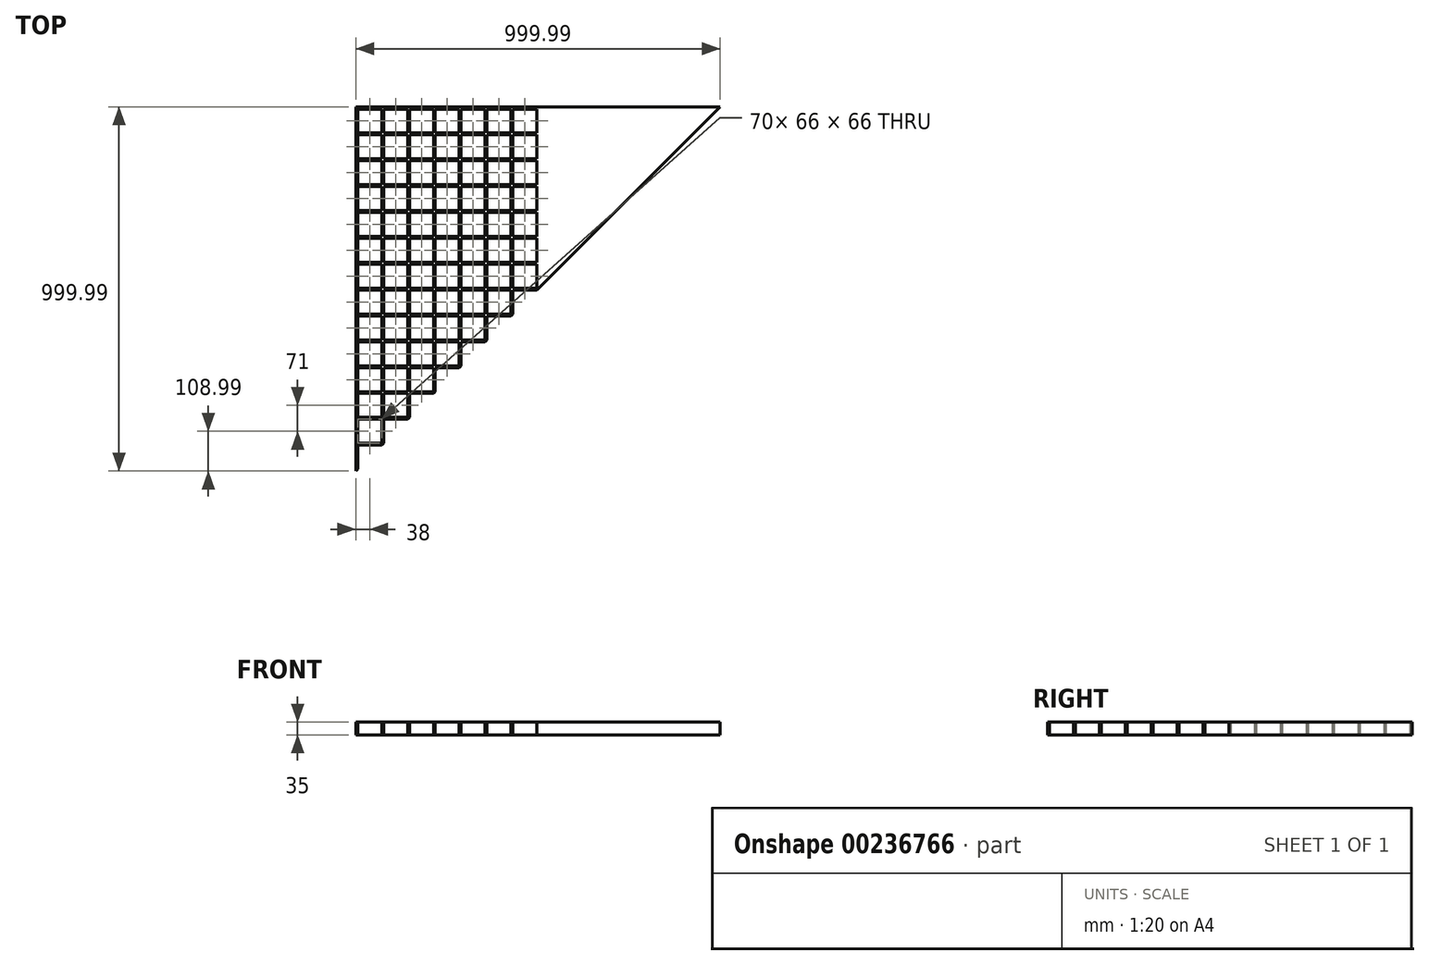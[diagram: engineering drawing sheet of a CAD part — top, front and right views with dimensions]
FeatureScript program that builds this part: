
annotation { "Feature Type Name" : "Feature", "Feature Type Description" : "" }
export const myFeature = defineFeature(function(context is Context, id is Id, definition is map)
    precondition{}
    {
        {
            var Q0;
            Q0=qCreatedBy(makeId("Top.planeOp"),FACE);
            var sketch = newSketch(context, id + "F0", { "sketchPlane" : qUnion([Q0])});
            skLineSegment(sketch, "E0.bottom", {"start": v(0, 0) * mm, "end": v(1000, 0) * mm});
            skLineSegment(sketch, "E0.top", {"start": v(0, 1000) * mm, "end": v(1000, 1000) * mm});
            skLineSegment(sketch, "E0.left", {"start": v(0, 0) * mm, "end": v(0, 1000) * mm});
            skLineSegment(sketch, "E0.right", {"start": v(1000, 0) * mm, "end": v(1000, 1000) * mm});
            skLineSegment(sketch, "E1.bottom", {"start": v(5, 5) * mm, "end": v(71, 5) * mm});
            skLineSegment(sketch, "E1.top", {"start": v(5, 71) * mm, "end": v(71, 71) * mm});
            skLineSegment(sketch, "E1.left", {"start": v(5, 5) * mm, "end": v(5, 71) * mm});
            skLineSegment(sketch, "E1.right", {"start": v(71, 5) * mm, "end": v(71, 71) * mm});
            skLineSegment(sketch, "E2.0.1.0", {"start": v(5, 142) * mm, "end": v(71, 142) * mm});
            skLineSegment(sketch, "E2.0.1.1", {"start": v(5, 76) * mm, "end": v(5, 142) * mm});
            skLineSegment(sketch, "E2.0.1.2", {"start": v(5, 76) * mm, "end": v(71, 76) * mm});
            skLineSegment(sketch, "E2.0.1.3", {"start": v(71, 76) * mm, "end": v(71, 142) * mm});
            skLineSegment(sketch, "E2.0.2.0", {"start": v(5, 213) * mm, "end": v(71, 213) * mm});
            skLineSegment(sketch, "E2.0.2.1", {"start": v(5, 147) * mm, "end": v(5, 213) * mm});
            skLineSegment(sketch, "E2.0.2.2", {"start": v(5, 147) * mm, "end": v(71, 147) * mm});
            skLineSegment(sketch, "E2.0.2.3", {"start": v(71, 147) * mm, "end": v(71, 213) * mm});
            skLineSegment(sketch, "E2.0.3.0", {"start": v(5, 284) * mm, "end": v(71, 284) * mm});
            skLineSegment(sketch, "E2.0.3.1", {"start": v(5, 218) * mm, "end": v(5, 284) * mm});
            skLineSegment(sketch, "E2.0.3.2", {"start": v(5, 218) * mm, "end": v(71, 218) * mm});
            skLineSegment(sketch, "E2.0.3.3", {"start": v(71, 218) * mm, "end": v(71, 284) * mm});
            skLineSegment(sketch, "E2.0.4.0", {"start": v(5, 355) * mm, "end": v(71, 355) * mm});
            skLineSegment(sketch, "E2.0.4.1", {"start": v(5, 289) * mm, "end": v(5, 355) * mm});
            skLineSegment(sketch, "E2.0.4.2", {"start": v(5, 289) * mm, "end": v(71, 289) * mm});
            skLineSegment(sketch, "E2.0.4.3", {"start": v(71, 289) * mm, "end": v(71, 355) * mm});
            skLineSegment(sketch, "E2.0.5.0", {"start": v(5, 426) * mm, "end": v(71, 426) * mm});
            skLineSegment(sketch, "E2.0.5.1", {"start": v(5, 360) * mm, "end": v(5, 426) * mm});
            skLineSegment(sketch, "E2.0.5.2", {"start": v(5, 360) * mm, "end": v(71, 360) * mm});
            skLineSegment(sketch, "E2.0.5.3", {"start": v(71, 360) * mm, "end": v(71, 426) * mm});
            skLineSegment(sketch, "E2.0.6.0", {"start": v(5, 497) * mm, "end": v(71, 497) * mm});
            skLineSegment(sketch, "E2.0.6.1", {"start": v(5, 431) * mm, "end": v(5, 497) * mm});
            skLineSegment(sketch, "E2.0.6.2", {"start": v(5, 431) * mm, "end": v(71, 431) * mm});
            skLineSegment(sketch, "E2.0.6.3", {"start": v(71, 431) * mm, "end": v(71, 497) * mm});
            skLineSegment(sketch, "E2.0.7.0", {"start": v(5, 568) * mm, "end": v(71, 568) * mm});
            skLineSegment(sketch, "E2.0.7.1", {"start": v(5, 502) * mm, "end": v(5, 568) * mm});
            skLineSegment(sketch, "E2.0.7.2", {"start": v(5, 502) * mm, "end": v(71, 502) * mm});
            skLineSegment(sketch, "E2.0.7.3", {"start": v(71, 502) * mm, "end": v(71, 568) * mm});
            skLineSegment(sketch, "E2.0.8.0", {"start": v(5, 639) * mm, "end": v(71, 639) * mm});
            skLineSegment(sketch, "E2.0.8.1", {"start": v(5, 573) * mm, "end": v(5, 639) * mm});
            skLineSegment(sketch, "E2.0.8.2", {"start": v(5, 573) * mm, "end": v(71, 573) * mm});
            skLineSegment(sketch, "E2.0.8.3", {"start": v(71, 573) * mm, "end": v(71, 639) * mm});
            skLineSegment(sketch, "E2.0.9.0", {"start": v(5, 710) * mm, "end": v(71, 710) * mm});
            skLineSegment(sketch, "E2.0.9.1", {"start": v(5, 644) * mm, "end": v(5, 710) * mm});
            skLineSegment(sketch, "E2.0.9.2", {"start": v(5, 644) * mm, "end": v(71, 644) * mm});
            skLineSegment(sketch, "E2.0.9.3", {"start": v(71, 644) * mm, "end": v(71, 710) * mm});
            skLineSegment(sketch, "E2.0.10.0", {"start": v(5, 781) * mm, "end": v(71, 781) * mm});
            skLineSegment(sketch, "E2.0.10.1", {"start": v(5, 715) * mm, "end": v(5, 781) * mm});
            skLineSegment(sketch, "E2.0.10.2", {"start": v(5, 715) * mm, "end": v(71, 715) * mm});
            skLineSegment(sketch, "E2.0.10.3", {"start": v(71, 715) * mm, "end": v(71, 781) * mm});
            skLineSegment(sketch, "E2.0.11.0", {"start": v(5, 852) * mm, "end": v(71, 852) * mm});
            skLineSegment(sketch, "E2.0.11.1", {"start": v(5, 786) * mm, "end": v(5, 852) * mm});
            skLineSegment(sketch, "E2.0.11.2", {"start": v(5, 786) * mm, "end": v(71, 786) * mm});
            skLineSegment(sketch, "E2.0.11.3", {"start": v(71, 786) * mm, "end": v(71, 852) * mm});
            skLineSegment(sketch, "E2.0.12.0", {"start": v(5, 923) * mm, "end": v(71, 923) * mm});
            skLineSegment(sketch, "E2.0.12.1", {"start": v(5, 857) * mm, "end": v(5, 923) * mm});
            skLineSegment(sketch, "E2.0.12.2", {"start": v(5, 857) * mm, "end": v(71, 857) * mm});
            skLineSegment(sketch, "E2.0.12.3", {"start": v(71, 857) * mm, "end": v(71, 923) * mm});
            skLineSegment(sketch, "E2.0.13.0", {"start": v(5, 994) * mm, "end": v(71, 994) * mm});
            skLineSegment(sketch, "E2.0.13.1", {"start": v(5, 928) * mm, "end": v(5, 994) * mm});
            skLineSegment(sketch, "E2.0.13.2", {"start": v(5, 928) * mm, "end": v(71, 928) * mm});
            skLineSegment(sketch, "E2.0.13.3", {"start": v(71, 928) * mm, "end": v(71, 994) * mm});
            skLineSegment(sketch, "E2.1.0.0", {"start": v(76, 71) * mm, "end": v(142, 71) * mm});
            skLineSegment(sketch, "E2.1.0.1", {"start": v(76, 5) * mm, "end": v(76, 71) * mm});
            skLineSegment(sketch, "E2.1.0.2", {"start": v(76, 5) * mm, "end": v(142, 5) * mm});
            skLineSegment(sketch, "E2.1.0.3", {"start": v(142, 5) * mm, "end": v(142, 71) * mm});
            skLineSegment(sketch, "E2.1.1.0", {"start": v(76, 142) * mm, "end": v(142, 142) * mm});
            skLineSegment(sketch, "E2.1.1.1", {"start": v(76, 76) * mm, "end": v(76, 142) * mm});
            skLineSegment(sketch, "E2.1.1.2", {"start": v(76, 76) * mm, "end": v(142, 76) * mm});
            skLineSegment(sketch, "E2.1.1.3", {"start": v(142, 76) * mm, "end": v(142, 142) * mm});
            skLineSegment(sketch, "E2.1.2.0", {"start": v(76, 213) * mm, "end": v(142, 213) * mm});
            skLineSegment(sketch, "E2.1.2.1", {"start": v(76, 147) * mm, "end": v(76, 213) * mm});
            skLineSegment(sketch, "E2.1.2.2", {"start": v(76, 147) * mm, "end": v(142, 147) * mm});
            skLineSegment(sketch, "E2.1.2.3", {"start": v(142, 147) * mm, "end": v(142, 213) * mm});
            skLineSegment(sketch, "E2.1.3.0", {"start": v(76, 284) * mm, "end": v(142, 284) * mm});
            skLineSegment(sketch, "E2.1.3.1", {"start": v(76, 218) * mm, "end": v(76, 284) * mm});
            skLineSegment(sketch, "E2.1.3.2", {"start": v(76, 218) * mm, "end": v(142, 218) * mm});
            skLineSegment(sketch, "E2.1.3.3", {"start": v(142, 218) * mm, "end": v(142, 284) * mm});
            skLineSegment(sketch, "E2.1.4.0", {"start": v(76, 355) * mm, "end": v(142, 355) * mm});
            skLineSegment(sketch, "E2.1.4.1", {"start": v(76, 289) * mm, "end": v(76, 355) * mm});
            skLineSegment(sketch, "E2.1.4.2", {"start": v(76, 289) * mm, "end": v(142, 289) * mm});
            skLineSegment(sketch, "E2.1.4.3", {"start": v(142, 289) * mm, "end": v(142, 355) * mm});
            skLineSegment(sketch, "E2.1.5.0", {"start": v(76, 426) * mm, "end": v(142, 426) * mm});
            skLineSegment(sketch, "E2.1.5.1", {"start": v(76, 360) * mm, "end": v(76, 426) * mm});
            skLineSegment(sketch, "E2.1.5.2", {"start": v(76, 360) * mm, "end": v(142, 360) * mm});
            skLineSegment(sketch, "E2.1.5.3", {"start": v(142, 360) * mm, "end": v(142, 426) * mm});
            skLineSegment(sketch, "E2.1.6.0", {"start": v(76, 497) * mm, "end": v(142, 497) * mm});
            skLineSegment(sketch, "E2.1.6.1", {"start": v(76, 431) * mm, "end": v(76, 497) * mm});
            skLineSegment(sketch, "E2.1.6.2", {"start": v(76, 431) * mm, "end": v(142, 431) * mm});
            skLineSegment(sketch, "E2.1.6.3", {"start": v(142, 431) * mm, "end": v(142, 497) * mm});
            skLineSegment(sketch, "E2.1.7.0", {"start": v(76, 568) * mm, "end": v(142, 568) * mm});
            skLineSegment(sketch, "E2.1.7.1", {"start": v(76, 502) * mm, "end": v(76, 568) * mm});
            skLineSegment(sketch, "E2.1.7.2", {"start": v(76, 502) * mm, "end": v(142, 502) * mm});
            skLineSegment(sketch, "E2.1.7.3", {"start": v(142, 502) * mm, "end": v(142, 568) * mm});
            skLineSegment(sketch, "E2.1.8.0", {"start": v(76, 639) * mm, "end": v(142, 639) * mm});
            skLineSegment(sketch, "E2.1.8.1", {"start": v(76, 573) * mm, "end": v(76, 639) * mm});
            skLineSegment(sketch, "E2.1.8.2", {"start": v(76, 573) * mm, "end": v(142, 573) * mm});
            skLineSegment(sketch, "E2.1.8.3", {"start": v(142, 573) * mm, "end": v(142, 639) * mm});
            skLineSegment(sketch, "E2.1.9.0", {"start": v(76, 710) * mm, "end": v(142, 710) * mm});
            skLineSegment(sketch, "E2.1.9.1", {"start": v(76, 644) * mm, "end": v(76, 710) * mm});
            skLineSegment(sketch, "E2.1.9.2", {"start": v(76, 644) * mm, "end": v(142, 644) * mm});
            skLineSegment(sketch, "E2.1.9.3", {"start": v(142, 644) * mm, "end": v(142, 710) * mm});
            skLineSegment(sketch, "E2.1.10.0", {"start": v(76, 781) * mm, "end": v(142, 781) * mm});
            skLineSegment(sketch, "E2.1.10.1", {"start": v(76, 715) * mm, "end": v(76, 781) * mm});
            skLineSegment(sketch, "E2.1.10.2", {"start": v(76, 715) * mm, "end": v(142, 715) * mm});
            skLineSegment(sketch, "E2.1.10.3", {"start": v(142, 715) * mm, "end": v(142, 781) * mm});
            skLineSegment(sketch, "E2.1.11.0", {"start": v(76, 852) * mm, "end": v(142, 852) * mm});
            skLineSegment(sketch, "E2.1.11.1", {"start": v(76, 786) * mm, "end": v(76, 852) * mm});
            skLineSegment(sketch, "E2.1.11.2", {"start": v(76, 786) * mm, "end": v(142, 786) * mm});
            skLineSegment(sketch, "E2.1.11.3", {"start": v(142, 786) * mm, "end": v(142, 852) * mm});
            skLineSegment(sketch, "E2.1.12.0", {"start": v(76, 923) * mm, "end": v(142, 923) * mm});
            skLineSegment(sketch, "E2.1.12.1", {"start": v(76, 857) * mm, "end": v(76, 923) * mm});
            skLineSegment(sketch, "E2.1.12.2", {"start": v(76, 857) * mm, "end": v(142, 857) * mm});
            skLineSegment(sketch, "E2.1.12.3", {"start": v(142, 857) * mm, "end": v(142, 923) * mm});
            skLineSegment(sketch, "E2.1.13.0", {"start": v(76, 994) * mm, "end": v(142, 994) * mm});
            skLineSegment(sketch, "E2.1.13.1", {"start": v(76, 928) * mm, "end": v(76, 994) * mm});
            skLineSegment(sketch, "E2.1.13.2", {"start": v(76, 928) * mm, "end": v(142, 928) * mm});
            skLineSegment(sketch, "E2.1.13.3", {"start": v(142, 928) * mm, "end": v(142, 994) * mm});
            skLineSegment(sketch, "E2.2.0.0", {"start": v(147, 71) * mm, "end": v(213, 71) * mm});
            skLineSegment(sketch, "E2.2.0.1", {"start": v(147, 5) * mm, "end": v(147, 71) * mm});
            skLineSegment(sketch, "E2.2.0.2", {"start": v(147, 5) * mm, "end": v(213, 5) * mm});
            skLineSegment(sketch, "E2.2.0.3", {"start": v(213, 5) * mm, "end": v(213, 71) * mm});
            skLineSegment(sketch, "E2.2.1.0", {"start": v(147, 142) * mm, "end": v(213, 142) * mm});
            skLineSegment(sketch, "E2.2.1.1", {"start": v(147, 76) * mm, "end": v(147, 142) * mm});
            skLineSegment(sketch, "E2.2.1.2", {"start": v(147, 76) * mm, "end": v(213, 76) * mm});
            skLineSegment(sketch, "E2.2.1.3", {"start": v(213, 76) * mm, "end": v(213, 142) * mm});
            skLineSegment(sketch, "E2.2.2.0", {"start": v(147, 213) * mm, "end": v(213, 213) * mm});
            skLineSegment(sketch, "E2.2.2.1", {"start": v(147, 147) * mm, "end": v(147, 213) * mm});
            skLineSegment(sketch, "E2.2.2.2", {"start": v(147, 147) * mm, "end": v(213, 147) * mm});
            skLineSegment(sketch, "E2.2.2.3", {"start": v(213, 147) * mm, "end": v(213, 213) * mm});
            skLineSegment(sketch, "E2.2.3.0", {"start": v(147, 284) * mm, "end": v(213, 284) * mm});
            skLineSegment(sketch, "E2.2.3.1", {"start": v(147, 218) * mm, "end": v(147, 284) * mm});
            skLineSegment(sketch, "E2.2.3.2", {"start": v(147, 218) * mm, "end": v(213, 218) * mm});
            skLineSegment(sketch, "E2.2.3.3", {"start": v(213, 218) * mm, "end": v(213, 284) * mm});
            skLineSegment(sketch, "E2.2.4.0", {"start": v(147, 355) * mm, "end": v(213, 355) * mm});
            skLineSegment(sketch, "E2.2.4.1", {"start": v(147, 289) * mm, "end": v(147, 355) * mm});
            skLineSegment(sketch, "E2.2.4.2", {"start": v(147, 289) * mm, "end": v(213, 289) * mm});
            skLineSegment(sketch, "E2.2.4.3", {"start": v(213, 289) * mm, "end": v(213, 355) * mm});
            skLineSegment(sketch, "E2.2.5.0", {"start": v(147, 426) * mm, "end": v(213, 426) * mm});
            skLineSegment(sketch, "E2.2.5.1", {"start": v(147, 360) * mm, "end": v(147, 426) * mm});
            skLineSegment(sketch, "E2.2.5.2", {"start": v(147, 360) * mm, "end": v(213, 360) * mm});
            skLineSegment(sketch, "E2.2.5.3", {"start": v(213, 360) * mm, "end": v(213, 426) * mm});
            skLineSegment(sketch, "E2.2.6.0", {"start": v(147, 497) * mm, "end": v(213, 497) * mm});
            skLineSegment(sketch, "E2.2.6.1", {"start": v(147, 431) * mm, "end": v(147, 497) * mm});
            skLineSegment(sketch, "E2.2.6.2", {"start": v(147, 431) * mm, "end": v(213, 431) * mm});
            skLineSegment(sketch, "E2.2.6.3", {"start": v(213, 431) * mm, "end": v(213, 497) * mm});
            skLineSegment(sketch, "E2.2.7.0", {"start": v(147, 568) * mm, "end": v(213, 568) * mm});
            skLineSegment(sketch, "E2.2.7.1", {"start": v(147, 502) * mm, "end": v(147, 568) * mm});
            skLineSegment(sketch, "E2.2.7.2", {"start": v(147, 502) * mm, "end": v(213, 502) * mm});
            skLineSegment(sketch, "E2.2.7.3", {"start": v(213, 502) * mm, "end": v(213, 568) * mm});
            skLineSegment(sketch, "E2.2.8.0", {"start": v(147, 639) * mm, "end": v(213, 639) * mm});
            skLineSegment(sketch, "E2.2.8.1", {"start": v(147, 573) * mm, "end": v(147, 639) * mm});
            skLineSegment(sketch, "E2.2.8.2", {"start": v(147, 573) * mm, "end": v(213, 573) * mm});
            skLineSegment(sketch, "E2.2.8.3", {"start": v(213, 573) * mm, "end": v(213, 639) * mm});
            skLineSegment(sketch, "E2.2.9.0", {"start": v(147, 710) * mm, "end": v(213, 710) * mm});
            skLineSegment(sketch, "E2.2.9.1", {"start": v(147, 644) * mm, "end": v(147, 710) * mm});
            skLineSegment(sketch, "E2.2.9.2", {"start": v(147, 644) * mm, "end": v(213, 644) * mm});
            skLineSegment(sketch, "E2.2.9.3", {"start": v(213, 644) * mm, "end": v(213, 710) * mm});
            skLineSegment(sketch, "E2.2.10.0", {"start": v(147, 781) * mm, "end": v(213, 781) * mm});
            skLineSegment(sketch, "E2.2.10.1", {"start": v(147, 715) * mm, "end": v(147, 781) * mm});
            skLineSegment(sketch, "E2.2.10.2", {"start": v(147, 715) * mm, "end": v(213, 715) * mm});
            skLineSegment(sketch, "E2.2.10.3", {"start": v(213, 715) * mm, "end": v(213, 781) * mm});
            skLineSegment(sketch, "E2.2.11.0", {"start": v(147, 852) * mm, "end": v(213, 852) * mm});
            skLineSegment(sketch, "E2.2.11.1", {"start": v(147, 786) * mm, "end": v(147, 852) * mm});
            skLineSegment(sketch, "E2.2.11.2", {"start": v(147, 786) * mm, "end": v(213, 786) * mm});
            skLineSegment(sketch, "E2.2.11.3", {"start": v(213, 786) * mm, "end": v(213, 852) * mm});
            skLineSegment(sketch, "E2.2.12.0", {"start": v(147, 923) * mm, "end": v(213, 923) * mm});
            skLineSegment(sketch, "E2.2.12.1", {"start": v(147, 857) * mm, "end": v(147, 923) * mm});
            skLineSegment(sketch, "E2.2.12.2", {"start": v(147, 857) * mm, "end": v(213, 857) * mm});
            skLineSegment(sketch, "E2.2.12.3", {"start": v(213, 857) * mm, "end": v(213, 923) * mm});
            skLineSegment(sketch, "E2.2.13.0", {"start": v(147, 994) * mm, "end": v(213, 994) * mm});
            skLineSegment(sketch, "E2.2.13.1", {"start": v(147, 928) * mm, "end": v(147, 994) * mm});
            skLineSegment(sketch, "E2.2.13.2", {"start": v(147, 928) * mm, "end": v(213, 928) * mm});
            skLineSegment(sketch, "E2.2.13.3", {"start": v(213, 928) * mm, "end": v(213, 994) * mm});
            skLineSegment(sketch, "E2.3.0.0", {"start": v(218, 71) * mm, "end": v(284, 71) * mm});
            skLineSegment(sketch, "E2.3.0.1", {"start": v(218, 5) * mm, "end": v(218, 71) * mm});
            skLineSegment(sketch, "E2.3.0.2", {"start": v(218, 5) * mm, "end": v(284, 5) * mm});
            skLineSegment(sketch, "E2.3.0.3", {"start": v(284, 5) * mm, "end": v(284, 71) * mm});
            skLineSegment(sketch, "E2.3.1.0", {"start": v(218, 142) * mm, "end": v(284, 142) * mm});
            skLineSegment(sketch, "E2.3.1.1", {"start": v(218, 76) * mm, "end": v(218, 142) * mm});
            skLineSegment(sketch, "E2.3.1.2", {"start": v(218, 76) * mm, "end": v(284, 76) * mm});
            skLineSegment(sketch, "E2.3.1.3", {"start": v(284, 76) * mm, "end": v(284, 142) * mm});
            skLineSegment(sketch, "E2.3.2.0", {"start": v(218, 213) * mm, "end": v(284, 213) * mm});
            skLineSegment(sketch, "E2.3.2.1", {"start": v(218, 147) * mm, "end": v(218, 213) * mm});
            skLineSegment(sketch, "E2.3.2.2", {"start": v(218, 147) * mm, "end": v(284, 147) * mm});
            skLineSegment(sketch, "E2.3.2.3", {"start": v(284, 147) * mm, "end": v(284, 213) * mm});
            skLineSegment(sketch, "E2.3.3.0", {"start": v(218, 284) * mm, "end": v(284, 284) * mm});
            skLineSegment(sketch, "E2.3.3.1", {"start": v(218, 218) * mm, "end": v(218, 284) * mm});
            skLineSegment(sketch, "E2.3.3.2", {"start": v(218, 218) * mm, "end": v(284, 218) * mm});
            skLineSegment(sketch, "E2.3.3.3", {"start": v(284, 218) * mm, "end": v(284, 284) * mm});
            skLineSegment(sketch, "E2.3.4.0", {"start": v(218, 355) * mm, "end": v(284, 355) * mm});
            skLineSegment(sketch, "E2.3.4.1", {"start": v(218, 289) * mm, "end": v(218, 355) * mm});
            skLineSegment(sketch, "E2.3.4.2", {"start": v(218, 289) * mm, "end": v(284, 289) * mm});
            skLineSegment(sketch, "E2.3.4.3", {"start": v(284, 289) * mm, "end": v(284, 355) * mm});
            skLineSegment(sketch, "E2.3.5.0", {"start": v(218, 426) * mm, "end": v(284, 426) * mm});
            skLineSegment(sketch, "E2.3.5.1", {"start": v(218, 360) * mm, "end": v(218, 426) * mm});
            skLineSegment(sketch, "E2.3.5.2", {"start": v(218, 360) * mm, "end": v(284, 360) * mm});
            skLineSegment(sketch, "E2.3.5.3", {"start": v(284, 360) * mm, "end": v(284, 426) * mm});
            skLineSegment(sketch, "E2.3.6.0", {"start": v(218, 497) * mm, "end": v(284, 497) * mm});
            skLineSegment(sketch, "E2.3.6.1", {"start": v(218, 431) * mm, "end": v(218, 497) * mm});
            skLineSegment(sketch, "E2.3.6.2", {"start": v(218, 431) * mm, "end": v(284, 431) * mm});
            skLineSegment(sketch, "E2.3.6.3", {"start": v(284, 431) * mm, "end": v(284, 497) * mm});
            skLineSegment(sketch, "E2.3.7.0", {"start": v(218, 568) * mm, "end": v(284, 568) * mm});
            skLineSegment(sketch, "E2.3.7.1", {"start": v(218, 502) * mm, "end": v(218, 568) * mm});
            skLineSegment(sketch, "E2.3.7.2", {"start": v(218, 502) * mm, "end": v(284, 502) * mm});
            skLineSegment(sketch, "E2.3.7.3", {"start": v(284, 502) * mm, "end": v(284, 568) * mm});
            skLineSegment(sketch, "E2.3.8.0", {"start": v(218, 639) * mm, "end": v(284, 639) * mm});
            skLineSegment(sketch, "E2.3.8.1", {"start": v(218, 573) * mm, "end": v(218, 639) * mm});
            skLineSegment(sketch, "E2.3.8.2", {"start": v(218, 573) * mm, "end": v(284, 573) * mm});
            skLineSegment(sketch, "E2.3.8.3", {"start": v(284, 573) * mm, "end": v(284, 639) * mm});
            skLineSegment(sketch, "E2.3.9.0", {"start": v(218, 710) * mm, "end": v(284, 710) * mm});
            skLineSegment(sketch, "E2.3.9.1", {"start": v(218, 644) * mm, "end": v(218, 710) * mm});
            skLineSegment(sketch, "E2.3.9.2", {"start": v(218, 644) * mm, "end": v(284, 644) * mm});
            skLineSegment(sketch, "E2.3.9.3", {"start": v(284, 644) * mm, "end": v(284, 710) * mm});
            skLineSegment(sketch, "E2.3.10.0", {"start": v(218, 781) * mm, "end": v(284, 781) * mm});
            skLineSegment(sketch, "E2.3.10.1", {"start": v(218, 715) * mm, "end": v(218, 781) * mm});
            skLineSegment(sketch, "E2.3.10.2", {"start": v(218, 715) * mm, "end": v(284, 715) * mm});
            skLineSegment(sketch, "E2.3.10.3", {"start": v(284, 715) * mm, "end": v(284, 781) * mm});
            skLineSegment(sketch, "E2.3.11.0", {"start": v(218, 852) * mm, "end": v(284, 852) * mm});
            skLineSegment(sketch, "E2.3.11.1", {"start": v(218, 786) * mm, "end": v(218, 852) * mm});
            skLineSegment(sketch, "E2.3.11.2", {"start": v(218, 786) * mm, "end": v(284, 786) * mm});
            skLineSegment(sketch, "E2.3.11.3", {"start": v(284, 786) * mm, "end": v(284, 852) * mm});
            skLineSegment(sketch, "E2.3.12.0", {"start": v(218, 923) * mm, "end": v(284, 923) * mm});
            skLineSegment(sketch, "E2.3.12.1", {"start": v(218, 857) * mm, "end": v(218, 923) * mm});
            skLineSegment(sketch, "E2.3.12.2", {"start": v(218, 857) * mm, "end": v(284, 857) * mm});
            skLineSegment(sketch, "E2.3.12.3", {"start": v(284, 857) * mm, "end": v(284, 923) * mm});
            skLineSegment(sketch, "E2.3.13.0", {"start": v(218, 994) * mm, "end": v(284, 994) * mm});
            skLineSegment(sketch, "E2.3.13.1", {"start": v(218, 928) * mm, "end": v(218, 994) * mm});
            skLineSegment(sketch, "E2.3.13.2", {"start": v(218, 928) * mm, "end": v(284, 928) * mm});
            skLineSegment(sketch, "E2.3.13.3", {"start": v(284, 928) * mm, "end": v(284, 994) * mm});
            skLineSegment(sketch, "E2.4.0.0", {"start": v(289, 71) * mm, "end": v(355, 71) * mm});
            skLineSegment(sketch, "E2.4.0.1", {"start": v(289, 5) * mm, "end": v(289, 71) * mm});
            skLineSegment(sketch, "E2.4.0.2", {"start": v(289, 5) * mm, "end": v(355, 5) * mm});
            skLineSegment(sketch, "E2.4.0.3", {"start": v(355, 5) * mm, "end": v(355, 71) * mm});
            skLineSegment(sketch, "E2.4.1.0", {"start": v(289, 142) * mm, "end": v(355, 142) * mm});
            skLineSegment(sketch, "E2.4.1.1", {"start": v(289, 76) * mm, "end": v(289, 142) * mm});
            skLineSegment(sketch, "E2.4.1.2", {"start": v(289, 76) * mm, "end": v(355, 76) * mm});
            skLineSegment(sketch, "E2.4.1.3", {"start": v(355, 76) * mm, "end": v(355, 142) * mm});
            skLineSegment(sketch, "E2.4.2.0", {"start": v(289, 213) * mm, "end": v(355, 213) * mm});
            skLineSegment(sketch, "E2.4.2.1", {"start": v(289, 147) * mm, "end": v(289, 213) * mm});
            skLineSegment(sketch, "E2.4.2.2", {"start": v(289, 147) * mm, "end": v(355, 147) * mm});
            skLineSegment(sketch, "E2.4.2.3", {"start": v(355, 147) * mm, "end": v(355, 213) * mm});
            skLineSegment(sketch, "E2.4.3.0", {"start": v(289, 284) * mm, "end": v(355, 284) * mm});
            skLineSegment(sketch, "E2.4.3.1", {"start": v(289, 218) * mm, "end": v(289, 284) * mm});
            skLineSegment(sketch, "E2.4.3.2", {"start": v(289, 218) * mm, "end": v(355, 218) * mm});
            skLineSegment(sketch, "E2.4.3.3", {"start": v(355, 218) * mm, "end": v(355, 284) * mm});
            skLineSegment(sketch, "E2.4.4.0", {"start": v(289, 355) * mm, "end": v(355, 355) * mm});
            skLineSegment(sketch, "E2.4.4.1", {"start": v(289, 289) * mm, "end": v(289, 355) * mm});
            skLineSegment(sketch, "E2.4.4.2", {"start": v(289, 289) * mm, "end": v(355, 289) * mm});
            skLineSegment(sketch, "E2.4.4.3", {"start": v(355, 289) * mm, "end": v(355, 355) * mm});
            skLineSegment(sketch, "E2.4.5.0", {"start": v(289, 426) * mm, "end": v(355, 426) * mm});
            skLineSegment(sketch, "E2.4.5.1", {"start": v(289, 360) * mm, "end": v(289, 426) * mm});
            skLineSegment(sketch, "E2.4.5.2", {"start": v(289, 360) * mm, "end": v(355, 360) * mm});
            skLineSegment(sketch, "E2.4.5.3", {"start": v(355, 360) * mm, "end": v(355, 426) * mm});
            skLineSegment(sketch, "E2.4.6.0", {"start": v(289, 497) * mm, "end": v(355, 497) * mm});
            skLineSegment(sketch, "E2.4.6.1", {"start": v(289, 431) * mm, "end": v(289, 497) * mm});
            skLineSegment(sketch, "E2.4.6.2", {"start": v(289, 431) * mm, "end": v(355, 431) * mm});
            skLineSegment(sketch, "E2.4.6.3", {"start": v(355, 431) * mm, "end": v(355, 497) * mm});
            skLineSegment(sketch, "E2.4.7.0", {"start": v(289, 568) * mm, "end": v(355, 568) * mm});
            skLineSegment(sketch, "E2.4.7.1", {"start": v(289, 502) * mm, "end": v(289, 568) * mm});
            skLineSegment(sketch, "E2.4.7.2", {"start": v(289, 502) * mm, "end": v(355, 502) * mm});
            skLineSegment(sketch, "E2.4.7.3", {"start": v(355, 502) * mm, "end": v(355, 568) * mm});
            skLineSegment(sketch, "E2.4.8.0", {"start": v(289, 639) * mm, "end": v(355, 639) * mm});
            skLineSegment(sketch, "E2.4.8.1", {"start": v(289, 573) * mm, "end": v(289, 639) * mm});
            skLineSegment(sketch, "E2.4.8.2", {"start": v(289, 573) * mm, "end": v(355, 573) * mm});
            skLineSegment(sketch, "E2.4.8.3", {"start": v(355, 573) * mm, "end": v(355, 639) * mm});
            skLineSegment(sketch, "E2.4.9.0", {"start": v(289, 710) * mm, "end": v(355, 710) * mm});
            skLineSegment(sketch, "E2.4.9.1", {"start": v(289, 644) * mm, "end": v(289, 710) * mm});
            skLineSegment(sketch, "E2.4.9.2", {"start": v(289, 644) * mm, "end": v(355, 644) * mm});
            skLineSegment(sketch, "E2.4.9.3", {"start": v(355, 644) * mm, "end": v(355, 710) * mm});
            skLineSegment(sketch, "E2.4.10.0", {"start": v(289, 781) * mm, "end": v(355, 781) * mm});
            skLineSegment(sketch, "E2.4.10.1", {"start": v(289, 715) * mm, "end": v(289, 781) * mm});
            skLineSegment(sketch, "E2.4.10.2", {"start": v(289, 715) * mm, "end": v(355, 715) * mm});
            skLineSegment(sketch, "E2.4.10.3", {"start": v(355, 715) * mm, "end": v(355, 781) * mm});
            skLineSegment(sketch, "E2.4.11.0", {"start": v(289, 852) * mm, "end": v(355, 852) * mm});
            skLineSegment(sketch, "E2.4.11.1", {"start": v(289, 786) * mm, "end": v(289, 852) * mm});
            skLineSegment(sketch, "E2.4.11.2", {"start": v(289, 786) * mm, "end": v(355, 786) * mm});
            skLineSegment(sketch, "E2.4.11.3", {"start": v(355, 786) * mm, "end": v(355, 852) * mm});
            skLineSegment(sketch, "E2.4.12.0", {"start": v(289, 923) * mm, "end": v(355, 923) * mm});
            skLineSegment(sketch, "E2.4.12.1", {"start": v(289, 857) * mm, "end": v(289, 923) * mm});
            skLineSegment(sketch, "E2.4.12.2", {"start": v(289, 857) * mm, "end": v(355, 857) * mm});
            skLineSegment(sketch, "E2.4.12.3", {"start": v(355, 857) * mm, "end": v(355, 923) * mm});
            skLineSegment(sketch, "E2.4.13.0", {"start": v(289, 994) * mm, "end": v(355, 994) * mm});
            skLineSegment(sketch, "E2.4.13.1", {"start": v(289, 928) * mm, "end": v(289, 994) * mm});
            skLineSegment(sketch, "E2.4.13.2", {"start": v(289, 928) * mm, "end": v(355, 928) * mm});
            skLineSegment(sketch, "E2.4.13.3", {"start": v(355, 928) * mm, "end": v(355, 994) * mm});
            skLineSegment(sketch, "E2.5.0.0", {"start": v(360, 71) * mm, "end": v(426, 71) * mm});
            skLineSegment(sketch, "E2.5.0.1", {"start": v(360, 5) * mm, "end": v(360, 71) * mm});
            skLineSegment(sketch, "E2.5.0.2", {"start": v(360, 5) * mm, "end": v(426, 5) * mm});
            skLineSegment(sketch, "E2.5.0.3", {"start": v(426, 5) * mm, "end": v(426, 71) * mm});
            skLineSegment(sketch, "E2.5.1.0", {"start": v(360, 142) * mm, "end": v(426, 142) * mm});
            skLineSegment(sketch, "E2.5.1.1", {"start": v(360, 76) * mm, "end": v(360, 142) * mm});
            skLineSegment(sketch, "E2.5.1.2", {"start": v(360, 76) * mm, "end": v(426, 76) * mm});
            skLineSegment(sketch, "E2.5.1.3", {"start": v(426, 76) * mm, "end": v(426, 142) * mm});
            skLineSegment(sketch, "E2.5.2.0", {"start": v(360, 213) * mm, "end": v(426, 213) * mm});
            skLineSegment(sketch, "E2.5.2.1", {"start": v(360, 147) * mm, "end": v(360, 213) * mm});
            skLineSegment(sketch, "E2.5.2.2", {"start": v(360, 147) * mm, "end": v(426, 147) * mm});
            skLineSegment(sketch, "E2.5.2.3", {"start": v(426, 147) * mm, "end": v(426, 213) * mm});
            skLineSegment(sketch, "E2.5.3.0", {"start": v(360, 284) * mm, "end": v(426, 284) * mm});
            skLineSegment(sketch, "E2.5.3.1", {"start": v(360, 218) * mm, "end": v(360, 284) * mm});
            skLineSegment(sketch, "E2.5.3.2", {"start": v(360, 218) * mm, "end": v(426, 218) * mm});
            skLineSegment(sketch, "E2.5.3.3", {"start": v(426, 218) * mm, "end": v(426, 284) * mm});
            skLineSegment(sketch, "E2.5.4.0", {"start": v(360, 355) * mm, "end": v(426, 355) * mm});
            skLineSegment(sketch, "E2.5.4.1", {"start": v(360, 289) * mm, "end": v(360, 355) * mm});
            skLineSegment(sketch, "E2.5.4.2", {"start": v(360, 289) * mm, "end": v(426, 289) * mm});
            skLineSegment(sketch, "E2.5.4.3", {"start": v(426, 289) * mm, "end": v(426, 355) * mm});
            skLineSegment(sketch, "E2.5.5.0", {"start": v(360, 426) * mm, "end": v(426, 426) * mm});
            skLineSegment(sketch, "E2.5.5.1", {"start": v(360, 360) * mm, "end": v(360, 426) * mm});
            skLineSegment(sketch, "E2.5.5.2", {"start": v(360, 360) * mm, "end": v(426, 360) * mm});
            skLineSegment(sketch, "E2.5.5.3", {"start": v(426, 360) * mm, "end": v(426, 426) * mm});
            skLineSegment(sketch, "E2.5.6.0", {"start": v(360, 497) * mm, "end": v(426, 497) * mm});
            skLineSegment(sketch, "E2.5.6.1", {"start": v(360, 431) * mm, "end": v(360, 497) * mm});
            skLineSegment(sketch, "E2.5.6.2", {"start": v(360, 431) * mm, "end": v(426, 431) * mm});
            skLineSegment(sketch, "E2.5.6.3", {"start": v(426, 431) * mm, "end": v(426, 497) * mm});
            skLineSegment(sketch, "E2.5.7.0", {"start": v(360, 568) * mm, "end": v(426, 568) * mm});
            skLineSegment(sketch, "E2.5.7.1", {"start": v(360, 502) * mm, "end": v(360, 568) * mm});
            skLineSegment(sketch, "E2.5.7.2", {"start": v(360, 502) * mm, "end": v(426, 502) * mm});
            skLineSegment(sketch, "E2.5.7.3", {"start": v(426, 502) * mm, "end": v(426, 568) * mm});
            skLineSegment(sketch, "E2.5.8.0", {"start": v(360, 639) * mm, "end": v(426, 639) * mm});
            skLineSegment(sketch, "E2.5.8.1", {"start": v(360, 573) * mm, "end": v(360, 639) * mm});
            skLineSegment(sketch, "E2.5.8.2", {"start": v(360, 573) * mm, "end": v(426, 573) * mm});
            skLineSegment(sketch, "E2.5.8.3", {"start": v(426, 573) * mm, "end": v(426, 639) * mm});
            skLineSegment(sketch, "E2.5.9.0", {"start": v(360, 710) * mm, "end": v(426, 710) * mm});
            skLineSegment(sketch, "E2.5.9.1", {"start": v(360, 644) * mm, "end": v(360, 710) * mm});
            skLineSegment(sketch, "E2.5.9.2", {"start": v(360, 644) * mm, "end": v(426, 644) * mm});
            skLineSegment(sketch, "E2.5.9.3", {"start": v(426, 644) * mm, "end": v(426, 710) * mm});
            skLineSegment(sketch, "E2.5.10.0", {"start": v(360, 781) * mm, "end": v(426, 781) * mm});
            skLineSegment(sketch, "E2.5.10.1", {"start": v(360, 715) * mm, "end": v(360, 781) * mm});
            skLineSegment(sketch, "E2.5.10.2", {"start": v(360, 715) * mm, "end": v(426, 715) * mm});
            skLineSegment(sketch, "E2.5.10.3", {"start": v(426, 715) * mm, "end": v(426, 781) * mm});
            skLineSegment(sketch, "E2.5.11.0", {"start": v(360, 852) * mm, "end": v(426, 852) * mm});
            skLineSegment(sketch, "E2.5.11.1", {"start": v(360, 786) * mm, "end": v(360, 852) * mm});
            skLineSegment(sketch, "E2.5.11.2", {"start": v(360, 786) * mm, "end": v(426, 786) * mm});
            skLineSegment(sketch, "E2.5.11.3", {"start": v(426, 786) * mm, "end": v(426, 852) * mm});
            skLineSegment(sketch, "E2.5.12.0", {"start": v(360, 923) * mm, "end": v(426, 923) * mm});
            skLineSegment(sketch, "E2.5.12.1", {"start": v(360, 857) * mm, "end": v(360, 923) * mm});
            skLineSegment(sketch, "E2.5.12.2", {"start": v(360, 857) * mm, "end": v(426, 857) * mm});
            skLineSegment(sketch, "E2.5.12.3", {"start": v(426, 857) * mm, "end": v(426, 923) * mm});
            skLineSegment(sketch, "E2.5.13.0", {"start": v(360, 994) * mm, "end": v(426, 994) * mm});
            skLineSegment(sketch, "E2.5.13.1", {"start": v(360, 928) * mm, "end": v(360, 994) * mm});
            skLineSegment(sketch, "E2.5.13.2", {"start": v(360, 928) * mm, "end": v(426, 928) * mm});
            skLineSegment(sketch, "E2.5.13.3", {"start": v(426, 928) * mm, "end": v(426, 994) * mm});
            skLineSegment(sketch, "E2.6.0.0", {"start": v(431, 71) * mm, "end": v(497, 71) * mm});
            skLineSegment(sketch, "E2.6.0.1", {"start": v(431, 5) * mm, "end": v(431, 71) * mm});
            skLineSegment(sketch, "E2.6.0.2", {"start": v(431, 5) * mm, "end": v(497, 5) * mm});
            skLineSegment(sketch, "E2.6.0.3", {"start": v(497, 5) * mm, "end": v(497, 71) * mm});
            skLineSegment(sketch, "E2.6.1.0", {"start": v(431, 142) * mm, "end": v(497, 142) * mm});
            skLineSegment(sketch, "E2.6.1.1", {"start": v(431, 76) * mm, "end": v(431, 142) * mm});
            skLineSegment(sketch, "E2.6.1.2", {"start": v(431, 76) * mm, "end": v(497, 76) * mm});
            skLineSegment(sketch, "E2.6.1.3", {"start": v(497, 76) * mm, "end": v(497, 142) * mm});
            skLineSegment(sketch, "E2.6.2.0", {"start": v(431, 213) * mm, "end": v(497, 213) * mm});
            skLineSegment(sketch, "E2.6.2.1", {"start": v(431, 147) * mm, "end": v(431, 213) * mm});
            skLineSegment(sketch, "E2.6.2.2", {"start": v(431, 147) * mm, "end": v(497, 147) * mm});
            skLineSegment(sketch, "E2.6.2.3", {"start": v(497, 147) * mm, "end": v(497, 213) * mm});
            skLineSegment(sketch, "E2.6.3.0", {"start": v(431, 284) * mm, "end": v(497, 284) * mm});
            skLineSegment(sketch, "E2.6.3.1", {"start": v(431, 218) * mm, "end": v(431, 284) * mm});
            skLineSegment(sketch, "E2.6.3.2", {"start": v(431, 218) * mm, "end": v(497, 218) * mm});
            skLineSegment(sketch, "E2.6.3.3", {"start": v(497, 218) * mm, "end": v(497, 284) * mm});
            skLineSegment(sketch, "E2.6.4.0", {"start": v(431, 355) * mm, "end": v(497, 355) * mm});
            skLineSegment(sketch, "E2.6.4.1", {"start": v(431, 289) * mm, "end": v(431, 355) * mm});
            skLineSegment(sketch, "E2.6.4.2", {"start": v(431, 289) * mm, "end": v(497, 289) * mm});
            skLineSegment(sketch, "E2.6.4.3", {"start": v(497, 289) * mm, "end": v(497, 355) * mm});
            skLineSegment(sketch, "E2.6.5.0", {"start": v(431, 426) * mm, "end": v(497, 426) * mm});
            skLineSegment(sketch, "E2.6.5.1", {"start": v(431, 360) * mm, "end": v(431, 426) * mm});
            skLineSegment(sketch, "E2.6.5.2", {"start": v(431, 360) * mm, "end": v(497, 360) * mm});
            skLineSegment(sketch, "E2.6.5.3", {"start": v(497, 360) * mm, "end": v(497, 426) * mm});
            skLineSegment(sketch, "E2.6.6.0", {"start": v(431, 497) * mm, "end": v(497, 497) * mm});
            skLineSegment(sketch, "E2.6.6.1", {"start": v(431, 431) * mm, "end": v(431, 497) * mm});
            skLineSegment(sketch, "E2.6.6.2", {"start": v(431, 431) * mm, "end": v(497, 431) * mm});
            skLineSegment(sketch, "E2.6.6.3", {"start": v(497, 431) * mm, "end": v(497, 497) * mm});
            skLineSegment(sketch, "E2.6.7.0", {"start": v(431, 568) * mm, "end": v(497, 568) * mm});
            skLineSegment(sketch, "E2.6.7.1", {"start": v(431, 502) * mm, "end": v(431, 568) * mm});
            skLineSegment(sketch, "E2.6.7.2", {"start": v(431, 502) * mm, "end": v(497, 502) * mm});
            skLineSegment(sketch, "E2.6.7.3", {"start": v(497, 502) * mm, "end": v(497, 568) * mm});
            skLineSegment(sketch, "E2.6.8.0", {"start": v(431, 639) * mm, "end": v(497, 639) * mm});
            skLineSegment(sketch, "E2.6.8.1", {"start": v(431, 573) * mm, "end": v(431, 639) * mm});
            skLineSegment(sketch, "E2.6.8.2", {"start": v(431, 573) * mm, "end": v(497, 573) * mm});
            skLineSegment(sketch, "E2.6.8.3", {"start": v(497, 573) * mm, "end": v(497, 639) * mm});
            skLineSegment(sketch, "E2.6.9.0", {"start": v(431, 710) * mm, "end": v(497, 710) * mm});
            skLineSegment(sketch, "E2.6.9.1", {"start": v(431, 644) * mm, "end": v(431, 710) * mm});
            skLineSegment(sketch, "E2.6.9.2", {"start": v(431, 644) * mm, "end": v(497, 644) * mm});
            skLineSegment(sketch, "E2.6.9.3", {"start": v(497, 644) * mm, "end": v(497, 710) * mm});
            skLineSegment(sketch, "E2.6.10.0", {"start": v(431, 781) * mm, "end": v(497, 781) * mm});
            skLineSegment(sketch, "E2.6.10.1", {"start": v(431, 715) * mm, "end": v(431, 781) * mm});
            skLineSegment(sketch, "E2.6.10.2", {"start": v(431, 715) * mm, "end": v(497, 715) * mm});
            skLineSegment(sketch, "E2.6.10.3", {"start": v(497, 715) * mm, "end": v(497, 781) * mm});
            skLineSegment(sketch, "E2.6.11.0", {"start": v(431, 852) * mm, "end": v(497, 852) * mm});
            skLineSegment(sketch, "E2.6.11.1", {"start": v(431, 786) * mm, "end": v(431, 852) * mm});
            skLineSegment(sketch, "E2.6.11.2", {"start": v(431, 786) * mm, "end": v(497, 786) * mm});
            skLineSegment(sketch, "E2.6.11.3", {"start": v(497, 786) * mm, "end": v(497, 852) * mm});
            skLineSegment(sketch, "E2.6.12.0", {"start": v(431, 923) * mm, "end": v(497, 923) * mm});
            skLineSegment(sketch, "E2.6.12.1", {"start": v(431, 857) * mm, "end": v(431, 923) * mm});
            skLineSegment(sketch, "E2.6.12.2", {"start": v(431, 857) * mm, "end": v(497, 857) * mm});
            skLineSegment(sketch, "E2.6.12.3", {"start": v(497, 857) * mm, "end": v(497, 923) * mm});
            skLineSegment(sketch, "E2.6.13.0", {"start": v(431, 994) * mm, "end": v(497, 994) * mm});
            skLineSegment(sketch, "E2.6.13.1", {"start": v(431, 928) * mm, "end": v(431, 994) * mm});
            skLineSegment(sketch, "E2.6.13.2", {"start": v(431, 928) * mm, "end": v(497, 928) * mm});
            skLineSegment(sketch, "E2.6.13.3", {"start": v(497, 928) * mm, "end": v(497, 994) * mm});
            skLineSegment(sketch, "E2.direction1", {"start": v(5, 71) * mm, "end": v(76, 71) * mm, "construction": true});
            skLineSegment(sketch, "E2.direction2", {"start": v(5, 71) * mm, "end": v(5, 142) * mm, "construction": true});
            skSolve(sketch);
        }
        {
            var Q0;
            Q0=makeQuery(id+"F0.imprint","IMPRINT",FACE,{"disambiguationData":[TD([[makeQuery(id+"F0.imprint","IMPRINT",EDGE,{"derivedFrom":sQuery(id+"F0.wireOp",EDGE,"E0.bottom")}),1.0]])]});
            extrude(context, id + "F1", {"entities" : qUnion([Q0]), "depth" : 35 * mm, "offsetDistance" : 25 * mm});
        }
        {
            var Q0;
            Q0=makeQuery(id+"F1.opExtrude","CAP_FACE",FACE,{"disambiguationData":[OSD([sQuery(id+"F0.wireOp",EDGE,"E0.bottom"),sQuery(id+"F0.wireOp",EDGE,"E0.top"),sQuery(id+"F0.wireOp",EDGE,"E0.left"),sQuery(id+"F0.wireOp",EDGE,"E0.right"),sQuery(id+"F0.wireOp",EDGE,"E1.bottom"),sQuery(id+"F0.wireOp",EDGE,"E1.top"),sQuery(id+"F0.wireOp",EDGE,"E1.left"),sQuery(id+"F0.wireOp",EDGE,"E1.right"),sQuery(id+"F0.wireOp",EDGE,"E2.0.1.0"),sQuery(id+"F0.wireOp",EDGE,"E2.0.1.1"),sQuery(id+"F0.wireOp",EDGE,"E2.0.1.2"),sQuery(id+"F0.wireOp",EDGE,"E2.0.1.3"),sQuery(id+"F0.wireOp",EDGE,"E2.0.2.0"),sQuery(id+"F0.wireOp",EDGE,"E2.0.2.1"),sQuery(id+"F0.wireOp",EDGE,"E2.0.2.2"),sQuery(id+"F0.wireOp",EDGE,"E2.0.2.3"),sQuery(id+"F0.wireOp",EDGE,"E2.0.3.0"),sQuery(id+"F0.wireOp",EDGE,"E2.0.3.1"),sQuery(id+"F0.wireOp",EDGE,"E2.0.3.2"),sQuery(id+"F0.wireOp",EDGE,"E2.0.3.3"),sQuery(id+"F0.wireOp",EDGE,"E2.0.4.0"),sQuery(id+"F0.wireOp",EDGE,"E2.0.4.1"),sQuery(id+"F0.wireOp",EDGE,"E2.0.4.2"),sQuery(id+"F0.wireOp",EDGE,"E2.0.4.3"),sQuery(id+"F0.wireOp",EDGE,"E2.0.5.0"),sQuery(id+"F0.wireOp",EDGE,"E2.0.5.1"),sQuery(id+"F0.wireOp",EDGE,"E2.0.5.2"),sQuery(id+"F0.wireOp",EDGE,"E2.0.5.3"),sQuery(id+"F0.wireOp",EDGE,"E2.0.6.0"),sQuery(id+"F0.wireOp",EDGE,"E2.0.6.1"),sQuery(id+"F0.wireOp",EDGE,"E2.0.6.2"),sQuery(id+"F0.wireOp",EDGE,"E2.0.6.3"),sQuery(id+"F0.wireOp",EDGE,"E2.0.7.0"),sQuery(id+"F0.wireOp",EDGE,"E2.0.7.1"),sQuery(id+"F0.wireOp",EDGE,"E2.0.7.2"),sQuery(id+"F0.wireOp",EDGE,"E2.0.7.3"),sQuery(id+"F0.wireOp",EDGE,"E2.0.8.0"),sQuery(id+"F0.wireOp",EDGE,"E2.0.8.1"),sQuery(id+"F0.wireOp",EDGE,"E2.0.8.2"),sQuery(id+"F0.wireOp",EDGE,"E2.0.8.3"),sQuery(id+"F0.wireOp",EDGE,"E2.0.9.0"),sQuery(id+"F0.wireOp",EDGE,"E2.0.9.1"),sQuery(id+"F0.wireOp",EDGE,"E2.0.9.2"),sQuery(id+"F0.wireOp",EDGE,"E2.0.9.3"),sQuery(id+"F0.wireOp",EDGE,"E2.0.10.0"),sQuery(id+"F0.wireOp",EDGE,"E2.0.10.1"),sQuery(id+"F0.wireOp",EDGE,"E2.0.10.2"),sQuery(id+"F0.wireOp",EDGE,"E2.0.10.3"),sQuery(id+"F0.wireOp",EDGE,"E2.0.11.0"),sQuery(id+"F0.wireOp",EDGE,"E2.0.11.1"),sQuery(id+"F0.wireOp",EDGE,"E2.0.11.2"),sQuery(id+"F0.wireOp",EDGE,"E2.0.11.3"),sQuery(id+"F0.wireOp",EDGE,"E2.0.12.0"),sQuery(id+"F0.wireOp",EDGE,"E2.0.12.1"),sQuery(id+"F0.wireOp",EDGE,"E2.0.12.2"),sQuery(id+"F0.wireOp",EDGE,"E2.0.12.3"),sQuery(id+"F0.wireOp",EDGE,"E2.0.13.0"),sQuery(id+"F0.wireOp",EDGE,"E2.0.13.1"),sQuery(id+"F0.wireOp",EDGE,"E2.0.13.2"),sQuery(id+"F0.wireOp",EDGE,"E2.0.13.3"),sQuery(id+"F0.wireOp",EDGE,"E2.1.0.0"),sQuery(id+"F0.wireOp",EDGE,"E2.1.0.1"),sQuery(id+"F0.wireOp",EDGE,"E2.1.0.2"),sQuery(id+"F0.wireOp",EDGE,"E2.1.0.3"),sQuery(id+"F0.wireOp",EDGE,"E2.1.1.0"),sQuery(id+"F0.wireOp",EDGE,"E2.1.1.1"),sQuery(id+"F0.wireOp",EDGE,"E2.1.1.2"),sQuery(id+"F0.wireOp",EDGE,"E2.1.1.3"),sQuery(id+"F0.wireOp",EDGE,"E2.1.2.0"),sQuery(id+"F0.wireOp",EDGE,"E2.1.2.1"),sQuery(id+"F0.wireOp",EDGE,"E2.1.2.2"),sQuery(id+"F0.wireOp",EDGE,"E2.1.2.3"),sQuery(id+"F0.wireOp",EDGE,"E2.1.3.0"),sQuery(id+"F0.wireOp",EDGE,"E2.1.3.1"),sQuery(id+"F0.wireOp",EDGE,"E2.1.3.2"),sQuery(id+"F0.wireOp",EDGE,"E2.1.3.3"),sQuery(id+"F0.wireOp",EDGE,"E2.1.4.0"),sQuery(id+"F0.wireOp",EDGE,"E2.1.4.1"),sQuery(id+"F0.wireOp",EDGE,"E2.1.4.2"),sQuery(id+"F0.wireOp",EDGE,"E2.1.4.3"),sQuery(id+"F0.wireOp",EDGE,"E2.1.5.0"),sQuery(id+"F0.wireOp",EDGE,"E2.1.5.1"),sQuery(id+"F0.wireOp",EDGE,"E2.1.5.2"),sQuery(id+"F0.wireOp",EDGE,"E2.1.5.3"),sQuery(id+"F0.wireOp",EDGE,"E2.1.6.0"),sQuery(id+"F0.wireOp",EDGE,"E2.1.6.1"),sQuery(id+"F0.wireOp",EDGE,"E2.1.6.2"),sQuery(id+"F0.wireOp",EDGE,"E2.1.6.3"),sQuery(id+"F0.wireOp",EDGE,"E2.1.7.0"),sQuery(id+"F0.wireOp",EDGE,"E2.1.7.1"),sQuery(id+"F0.wireOp",EDGE,"E2.1.7.2"),sQuery(id+"F0.wireOp",EDGE,"E2.1.7.3"),sQuery(id+"F0.wireOp",EDGE,"E2.1.8.0"),sQuery(id+"F0.wireOp",EDGE,"E2.1.8.1"),sQuery(id+"F0.wireOp",EDGE,"E2.1.8.2"),sQuery(id+"F0.wireOp",EDGE,"E2.1.8.3"),sQuery(id+"F0.wireOp",EDGE,"E2.1.9.0"),sQuery(id+"F0.wireOp",EDGE,"E2.1.9.1"),sQuery(id+"F0.wireOp",EDGE,"E2.1.9.2"),sQuery(id+"F0.wireOp",EDGE,"E2.1.9.3"),sQuery(id+"F0.wireOp",EDGE,"E2.1.10.0"),sQuery(id+"F0.wireOp",EDGE,"E2.1.10.1"),sQuery(id+"F0.wireOp",EDGE,"E2.1.10.2"),sQuery(id+"F0.wireOp",EDGE,"E2.1.10.3"),sQuery(id+"F0.wireOp",EDGE,"E2.1.11.0"),sQuery(id+"F0.wireOp",EDGE,"E2.1.11.1"),sQuery(id+"F0.wireOp",EDGE,"E2.1.11.2"),sQuery(id+"F0.wireOp",EDGE,"E2.1.11.3"),sQuery(id+"F0.wireOp",EDGE,"E2.1.12.0"),sQuery(id+"F0.wireOp",EDGE,"E2.1.12.1"),sQuery(id+"F0.wireOp",EDGE,"E2.1.12.2"),sQuery(id+"F0.wireOp",EDGE,"E2.1.12.3"),sQuery(id+"F0.wireOp",EDGE,"E2.1.13.0"),sQuery(id+"F0.wireOp",EDGE,"E2.1.13.1"),sQuery(id+"F0.wireOp",EDGE,"E2.1.13.2"),sQuery(id+"F0.wireOp",EDGE,"E2.1.13.3"),sQuery(id+"F0.wireOp",EDGE,"E2.2.0.0"),sQuery(id+"F0.wireOp",EDGE,"E2.2.0.1"),sQuery(id+"F0.wireOp",EDGE,"E2.2.0.2"),sQuery(id+"F0.wireOp",EDGE,"E2.2.0.3"),sQuery(id+"F0.wireOp",EDGE,"E2.2.1.0"),sQuery(id+"F0.wireOp",EDGE,"E2.2.1.1"),sQuery(id+"F0.wireOp",EDGE,"E2.2.1.2"),sQuery(id+"F0.wireOp",EDGE,"E2.2.1.3"),sQuery(id+"F0.wireOp",EDGE,"E2.2.2.0"),sQuery(id+"F0.wireOp",EDGE,"E2.2.2.1"),sQuery(id+"F0.wireOp",EDGE,"E2.2.2.2"),sQuery(id+"F0.wireOp",EDGE,"E2.2.2.3"),sQuery(id+"F0.wireOp",EDGE,"E2.2.3.0"),sQuery(id+"F0.wireOp",EDGE,"E2.2.3.1"),sQuery(id+"F0.wireOp",EDGE,"E2.2.3.2"),sQuery(id+"F0.wireOp",EDGE,"E2.2.3.3"),sQuery(id+"F0.wireOp",EDGE,"E2.2.4.0"),sQuery(id+"F0.wireOp",EDGE,"E2.2.4.1"),sQuery(id+"F0.wireOp",EDGE,"E2.2.4.2"),sQuery(id+"F0.wireOp",EDGE,"E2.2.4.3"),sQuery(id+"F0.wireOp",EDGE,"E2.2.5.0"),sQuery(id+"F0.wireOp",EDGE,"E2.2.5.1"),sQuery(id+"F0.wireOp",EDGE,"E2.2.5.2"),sQuery(id+"F0.wireOp",EDGE,"E2.2.5.3"),sQuery(id+"F0.wireOp",EDGE,"E2.2.6.0"),sQuery(id+"F0.wireOp",EDGE,"E2.2.6.1"),sQuery(id+"F0.wireOp",EDGE,"E2.2.6.2"),sQuery(id+"F0.wireOp",EDGE,"E2.2.6.3"),sQuery(id+"F0.wireOp",EDGE,"E2.2.7.0"),sQuery(id+"F0.wireOp",EDGE,"E2.2.7.1"),sQuery(id+"F0.wireOp",EDGE,"E2.2.7.2"),sQuery(id+"F0.wireOp",EDGE,"E2.2.7.3"),sQuery(id+"F0.wireOp",EDGE,"E2.2.8.0"),sQuery(id+"F0.wireOp",EDGE,"E2.2.8.1"),sQuery(id+"F0.wireOp",EDGE,"E2.2.8.2"),sQuery(id+"F0.wireOp",EDGE,"E2.2.8.3"),sQuery(id+"F0.wireOp",EDGE,"E2.2.9.0"),sQuery(id+"F0.wireOp",EDGE,"E2.2.9.1"),sQuery(id+"F0.wireOp",EDGE,"E2.2.9.2"),sQuery(id+"F0.wireOp",EDGE,"E2.2.9.3"),sQuery(id+"F0.wireOp",EDGE,"E2.2.10.0"),sQuery(id+"F0.wireOp",EDGE,"E2.2.10.1"),sQuery(id+"F0.wireOp",EDGE,"E2.2.10.2"),sQuery(id+"F0.wireOp",EDGE,"E2.2.10.3"),sQuery(id+"F0.wireOp",EDGE,"E2.2.11.0"),sQuery(id+"F0.wireOp",EDGE,"E2.2.11.1"),sQuery(id+"F0.wireOp",EDGE,"E2.2.11.2"),sQuery(id+"F0.wireOp",EDGE,"E2.2.11.3"),sQuery(id+"F0.wireOp",EDGE,"E2.2.12.0"),sQuery(id+"F0.wireOp",EDGE,"E2.2.12.1"),sQuery(id+"F0.wireOp",EDGE,"E2.2.12.2"),sQuery(id+"F0.wireOp",EDGE,"E2.2.12.3"),sQuery(id+"F0.wireOp",EDGE,"E2.2.13.0"),sQuery(id+"F0.wireOp",EDGE,"E2.2.13.1"),sQuery(id+"F0.wireOp",EDGE,"E2.2.13.2"),sQuery(id+"F0.wireOp",EDGE,"E2.2.13.3"),sQuery(id+"F0.wireOp",EDGE,"E2.3.0.0"),sQuery(id+"F0.wireOp",EDGE,"E2.3.0.1"),sQuery(id+"F0.wireOp",EDGE,"E2.3.0.2"),sQuery(id+"F0.wireOp",EDGE,"E2.3.0.3"),sQuery(id+"F0.wireOp",EDGE,"E2.3.1.0"),sQuery(id+"F0.wireOp",EDGE,"E2.3.1.1"),sQuery(id+"F0.wireOp",EDGE,"E2.3.1.2"),sQuery(id+"F0.wireOp",EDGE,"E2.3.1.3"),sQuery(id+"F0.wireOp",EDGE,"E2.3.2.0"),sQuery(id+"F0.wireOp",EDGE,"E2.3.2.1"),sQuery(id+"F0.wireOp",EDGE,"E2.3.2.2"),sQuery(id+"F0.wireOp",EDGE,"E2.3.2.3"),sQuery(id+"F0.wireOp",EDGE,"E2.3.3.0"),sQuery(id+"F0.wireOp",EDGE,"E2.3.3.1"),sQuery(id+"F0.wireOp",EDGE,"E2.3.3.2"),sQuery(id+"F0.wireOp",EDGE,"E2.3.3.3"),sQuery(id+"F0.wireOp",EDGE,"E2.3.4.0"),sQuery(id+"F0.wireOp",EDGE,"E2.3.4.1"),sQuery(id+"F0.wireOp",EDGE,"E2.3.4.2"),sQuery(id+"F0.wireOp",EDGE,"E2.3.4.3"),sQuery(id+"F0.wireOp",EDGE,"E2.3.5.0"),sQuery(id+"F0.wireOp",EDGE,"E2.3.5.1"),sQuery(id+"F0.wireOp",EDGE,"E2.3.5.2"),sQuery(id+"F0.wireOp",EDGE,"E2.3.5.3"),sQuery(id+"F0.wireOp",EDGE,"E2.3.6.0"),sQuery(id+"F0.wireOp",EDGE,"E2.3.6.1"),sQuery(id+"F0.wireOp",EDGE,"E2.3.6.2"),sQuery(id+"F0.wireOp",EDGE,"E2.3.6.3"),sQuery(id+"F0.wireOp",EDGE,"E2.3.7.0"),sQuery(id+"F0.wireOp",EDGE,"E2.3.7.1"),sQuery(id+"F0.wireOp",EDGE,"E2.3.7.2"),sQuery(id+"F0.wireOp",EDGE,"E2.3.7.3"),sQuery(id+"F0.wireOp",EDGE,"E2.3.8.0"),sQuery(id+"F0.wireOp",EDGE,"E2.3.8.1"),sQuery(id+"F0.wireOp",EDGE,"E2.3.8.2"),sQuery(id+"F0.wireOp",EDGE,"E2.3.8.3"),sQuery(id+"F0.wireOp",EDGE,"E2.3.9.0"),sQuery(id+"F0.wireOp",EDGE,"E2.3.9.1"),sQuery(id+"F0.wireOp",EDGE,"E2.3.9.2"),sQuery(id+"F0.wireOp",EDGE,"E2.3.9.3"),sQuery(id+"F0.wireOp",EDGE,"E2.3.10.0"),sQuery(id+"F0.wireOp",EDGE,"E2.3.10.1"),sQuery(id+"F0.wireOp",EDGE,"E2.3.10.2"),sQuery(id+"F0.wireOp",EDGE,"E2.3.10.3"),sQuery(id+"F0.wireOp",EDGE,"E2.3.11.0"),sQuery(id+"F0.wireOp",EDGE,"E2.3.11.1"),sQuery(id+"F0.wireOp",EDGE,"E2.3.11.2"),sQuery(id+"F0.wireOp",EDGE,"E2.3.11.3"),sQuery(id+"F0.wireOp",EDGE,"E2.3.12.0"),sQuery(id+"F0.wireOp",EDGE,"E2.3.12.1"),sQuery(id+"F0.wireOp",EDGE,"E2.3.12.2"),sQuery(id+"F0.wireOp",EDGE,"E2.3.12.3"),sQuery(id+"F0.wireOp",EDGE,"E2.3.13.0"),sQuery(id+"F0.wireOp",EDGE,"E2.3.13.1"),sQuery(id+"F0.wireOp",EDGE,"E2.3.13.2"),sQuery(id+"F0.wireOp",EDGE,"E2.3.13.3"),sQuery(id+"F0.wireOp",EDGE,"E2.4.0.0"),sQuery(id+"F0.wireOp",EDGE,"E2.4.0.1"),sQuery(id+"F0.wireOp",EDGE,"E2.4.0.2"),sQuery(id+"F0.wireOp",EDGE,"E2.4.0.3"),sQuery(id+"F0.wireOp",EDGE,"E2.4.1.0"),sQuery(id+"F0.wireOp",EDGE,"E2.4.1.1"),sQuery(id+"F0.wireOp",EDGE,"E2.4.1.2"),sQuery(id+"F0.wireOp",EDGE,"E2.4.1.3"),sQuery(id+"F0.wireOp",EDGE,"E2.4.2.0"),sQuery(id+"F0.wireOp",EDGE,"E2.4.2.1"),sQuery(id+"F0.wireOp",EDGE,"E2.4.2.2"),sQuery(id+"F0.wireOp",EDGE,"E2.4.2.3"),sQuery(id+"F0.wireOp",EDGE,"E2.4.3.0"),sQuery(id+"F0.wireOp",EDGE,"E2.4.3.1"),sQuery(id+"F0.wireOp",EDGE,"E2.4.3.2"),sQuery(id+"F0.wireOp",EDGE,"E2.4.3.3"),sQuery(id+"F0.wireOp",EDGE,"E2.4.4.0"),sQuery(id+"F0.wireOp",EDGE,"E2.4.4.1"),sQuery(id+"F0.wireOp",EDGE,"E2.4.4.2"),sQuery(id+"F0.wireOp",EDGE,"E2.4.4.3"),sQuery(id+"F0.wireOp",EDGE,"E2.4.5.0"),sQuery(id+"F0.wireOp",EDGE,"E2.4.5.1"),sQuery(id+"F0.wireOp",EDGE,"E2.4.5.2"),sQuery(id+"F0.wireOp",EDGE,"E2.4.5.3"),sQuery(id+"F0.wireOp",EDGE,"E2.4.6.0"),sQuery(id+"F0.wireOp",EDGE,"E2.4.6.1"),sQuery(id+"F0.wireOp",EDGE,"E2.4.6.2"),sQuery(id+"F0.wireOp",EDGE,"E2.4.6.3"),sQuery(id+"F0.wireOp",EDGE,"E2.4.7.0"),sQuery(id+"F0.wireOp",EDGE,"E2.4.7.1"),sQuery(id+"F0.wireOp",EDGE,"E2.4.7.2"),sQuery(id+"F0.wireOp",EDGE,"E2.4.7.3"),sQuery(id+"F0.wireOp",EDGE,"E2.4.8.0"),sQuery(id+"F0.wireOp",EDGE,"E2.4.8.1"),sQuery(id+"F0.wireOp",EDGE,"E2.4.8.2"),sQuery(id+"F0.wireOp",EDGE,"E2.4.8.3"),sQuery(id+"F0.wireOp",EDGE,"E2.4.9.0"),sQuery(id+"F0.wireOp",EDGE,"E2.4.9.1"),sQuery(id+"F0.wireOp",EDGE,"E2.4.9.2"),sQuery(id+"F0.wireOp",EDGE,"E2.4.9.3"),sQuery(id+"F0.wireOp",EDGE,"E2.4.10.0"),sQuery(id+"F0.wireOp",EDGE,"E2.4.10.1"),sQuery(id+"F0.wireOp",EDGE,"E2.4.10.2"),sQuery(id+"F0.wireOp",EDGE,"E2.4.10.3"),sQuery(id+"F0.wireOp",EDGE,"E2.4.11.0"),sQuery(id+"F0.wireOp",EDGE,"E2.4.11.1"),sQuery(id+"F0.wireOp",EDGE,"E2.4.11.2"),sQuery(id+"F0.wireOp",EDGE,"E2.4.11.3"),sQuery(id+"F0.wireOp",EDGE,"E2.4.12.0"),sQuery(id+"F0.wireOp",EDGE,"E2.4.12.1"),sQuery(id+"F0.wireOp",EDGE,"E2.4.12.2"),sQuery(id+"F0.wireOp",EDGE,"E2.4.12.3"),sQuery(id+"F0.wireOp",EDGE,"E2.4.13.0"),sQuery(id+"F0.wireOp",EDGE,"E2.4.13.1"),sQuery(id+"F0.wireOp",EDGE,"E2.4.13.2"),sQuery(id+"F0.wireOp",EDGE,"E2.4.13.3"),sQuery(id+"F0.wireOp",EDGE,"E2.5.0.0"),sQuery(id+"F0.wireOp",EDGE,"E2.5.0.1"),sQuery(id+"F0.wireOp",EDGE,"E2.5.0.2"),sQuery(id+"F0.wireOp",EDGE,"E2.5.0.3"),sQuery(id+"F0.wireOp",EDGE,"E2.5.1.0"),sQuery(id+"F0.wireOp",EDGE,"E2.5.1.1"),sQuery(id+"F0.wireOp",EDGE,"E2.5.1.2"),sQuery(id+"F0.wireOp",EDGE,"E2.5.1.3"),sQuery(id+"F0.wireOp",EDGE,"E2.5.2.0"),sQuery(id+"F0.wireOp",EDGE,"E2.5.2.1"),sQuery(id+"F0.wireOp",EDGE,"E2.5.2.2"),sQuery(id+"F0.wireOp",EDGE,"E2.5.2.3"),sQuery(id+"F0.wireOp",EDGE,"E2.5.3.0"),sQuery(id+"F0.wireOp",EDGE,"E2.5.3.1"),sQuery(id+"F0.wireOp",EDGE,"E2.5.3.2"),sQuery(id+"F0.wireOp",EDGE,"E2.5.3.3"),sQuery(id+"F0.wireOp",EDGE,"E2.5.4.0"),sQuery(id+"F0.wireOp",EDGE,"E2.5.4.1"),sQuery(id+"F0.wireOp",EDGE,"E2.5.4.2"),sQuery(id+"F0.wireOp",EDGE,"E2.5.4.3"),sQuery(id+"F0.wireOp",EDGE,"E2.5.5.0"),sQuery(id+"F0.wireOp",EDGE,"E2.5.5.1"),sQuery(id+"F0.wireOp",EDGE,"E2.5.5.2"),sQuery(id+"F0.wireOp",EDGE,"E2.5.5.3"),sQuery(id+"F0.wireOp",EDGE,"E2.5.6.0"),sQuery(id+"F0.wireOp",EDGE,"E2.5.6.1"),sQuery(id+"F0.wireOp",EDGE,"E2.5.6.2"),sQuery(id+"F0.wireOp",EDGE,"E2.5.6.3"),sQuery(id+"F0.wireOp",EDGE,"E2.5.7.0"),sQuery(id+"F0.wireOp",EDGE,"E2.5.7.1"),sQuery(id+"F0.wireOp",EDGE,"E2.5.7.2"),sQuery(id+"F0.wireOp",EDGE,"E2.5.7.3"),sQuery(id+"F0.wireOp",EDGE,"E2.5.8.0"),sQuery(id+"F0.wireOp",EDGE,"E2.5.8.1"),sQuery(id+"F0.wireOp",EDGE,"E2.5.8.2"),sQuery(id+"F0.wireOp",EDGE,"E2.5.8.3"),sQuery(id+"F0.wireOp",EDGE,"E2.5.9.0"),sQuery(id+"F0.wireOp",EDGE,"E2.5.9.1"),sQuery(id+"F0.wireOp",EDGE,"E2.5.9.2"),sQuery(id+"F0.wireOp",EDGE,"E2.5.9.3"),sQuery(id+"F0.wireOp",EDGE,"E2.5.10.0"),sQuery(id+"F0.wireOp",EDGE,"E2.5.10.1"),sQuery(id+"F0.wireOp",EDGE,"E2.5.10.2"),sQuery(id+"F0.wireOp",EDGE,"E2.5.10.3"),sQuery(id+"F0.wireOp",EDGE,"E2.5.11.0"),sQuery(id+"F0.wireOp",EDGE,"E2.5.11.1"),sQuery(id+"F0.wireOp",EDGE,"E2.5.11.2"),sQuery(id+"F0.wireOp",EDGE,"E2.5.11.3"),sQuery(id+"F0.wireOp",EDGE,"E2.5.12.0"),sQuery(id+"F0.wireOp",EDGE,"E2.5.12.1"),sQuery(id+"F0.wireOp",EDGE,"E2.5.12.2"),sQuery(id+"F0.wireOp",EDGE,"E2.5.12.3"),sQuery(id+"F0.wireOp",EDGE,"E2.5.13.0"),sQuery(id+"F0.wireOp",EDGE,"E2.5.13.1"),sQuery(id+"F0.wireOp",EDGE,"E2.5.13.2"),sQuery(id+"F0.wireOp",EDGE,"E2.5.13.3"),sQuery(id+"F0.wireOp",EDGE,"E2.6.0.0"),sQuery(id+"F0.wireOp",EDGE,"E2.6.0.1"),sQuery(id+"F0.wireOp",EDGE,"E2.6.0.2"),sQuery(id+"F0.wireOp",EDGE,"E2.6.0.3"),sQuery(id+"F0.wireOp",EDGE,"E2.6.1.0"),sQuery(id+"F0.wireOp",EDGE,"E2.6.1.1"),sQuery(id+"F0.wireOp",EDGE,"E2.6.1.2"),sQuery(id+"F0.wireOp",EDGE,"E2.6.1.3"),sQuery(id+"F0.wireOp",EDGE,"E2.6.2.0"),sQuery(id+"F0.wireOp",EDGE,"E2.6.2.1"),sQuery(id+"F0.wireOp",EDGE,"E2.6.2.2"),sQuery(id+"F0.wireOp",EDGE,"E2.6.2.3"),sQuery(id+"F0.wireOp",EDGE,"E2.6.3.0"),sQuery(id+"F0.wireOp",EDGE,"E2.6.3.1"),sQuery(id+"F0.wireOp",EDGE,"E2.6.3.2"),sQuery(id+"F0.wireOp",EDGE,"E2.6.3.3"),sQuery(id+"F0.wireOp",EDGE,"E2.6.4.0"),sQuery(id+"F0.wireOp",EDGE,"E2.6.4.1"),sQuery(id+"F0.wireOp",EDGE,"E2.6.4.2"),sQuery(id+"F0.wireOp",EDGE,"E2.6.4.3"),sQuery(id+"F0.wireOp",EDGE,"E2.6.5.0"),sQuery(id+"F0.wireOp",EDGE,"E2.6.5.1"),sQuery(id+"F0.wireOp",EDGE,"E2.6.5.2"),sQuery(id+"F0.wireOp",EDGE,"E2.6.5.3"),sQuery(id+"F0.wireOp",EDGE,"E2.6.6.0"),sQuery(id+"F0.wireOp",EDGE,"E2.6.6.1"),sQuery(id+"F0.wireOp",EDGE,"E2.6.6.2"),sQuery(id+"F0.wireOp",EDGE,"E2.6.6.3"),sQuery(id+"F0.wireOp",EDGE,"E2.6.7.0"),sQuery(id+"F0.wireOp",EDGE,"E2.6.7.1"),sQuery(id+"F0.wireOp",EDGE,"E2.6.7.2"),sQuery(id+"F0.wireOp",EDGE,"E2.6.7.3"),sQuery(id+"F0.wireOp",EDGE,"E2.6.8.0"),sQuery(id+"F0.wireOp",EDGE,"E2.6.8.1"),sQuery(id+"F0.wireOp",EDGE,"E2.6.8.2"),sQuery(id+"F0.wireOp",EDGE,"E2.6.8.3"),sQuery(id+"F0.wireOp",EDGE,"E2.6.9.0"),sQuery(id+"F0.wireOp",EDGE,"E2.6.9.1"),sQuery(id+"F0.wireOp",EDGE,"E2.6.9.2"),sQuery(id+"F0.wireOp",EDGE,"E2.6.9.3"),sQuery(id+"F0.wireOp",EDGE,"E2.6.10.0"),sQuery(id+"F0.wireOp",EDGE,"E2.6.10.1"),sQuery(id+"F0.wireOp",EDGE,"E2.6.10.2"),sQuery(id+"F0.wireOp",EDGE,"E2.6.10.3"),sQuery(id+"F0.wireOp",EDGE,"E2.6.11.0"),sQuery(id+"F0.wireOp",EDGE,"E2.6.11.1"),sQuery(id+"F0.wireOp",EDGE,"E2.6.11.2"),sQuery(id+"F0.wireOp",EDGE,"E2.6.11.3"),sQuery(id+"F0.wireOp",EDGE,"E2.6.12.0"),sQuery(id+"F0.wireOp",EDGE,"E2.6.12.1"),sQuery(id+"F0.wireOp",EDGE,"E2.6.12.2"),sQuery(id+"F0.wireOp",EDGE,"E2.6.12.3"),sQuery(id+"F0.wireOp",EDGE,"E2.6.13.0"),sQuery(id+"F0.wireOp",EDGE,"E2.6.13.1"),sQuery(id+"F0.wireOp",EDGE,"E2.6.13.2"),sQuery(id+"F0.wireOp",EDGE,"E2.6.13.3"),sQuery(id+"F0.wireOp",EDGE,"E2.7.0.0"),sQuery(id+"F0.wireOp",EDGE,"E2.7.0.1"),sQuery(id+"F0.wireOp",EDGE,"E2.7.0.2"),sQuery(id+"F0.wireOp",EDGE,"E2.7.0.3"),sQuery(id+"F0.wireOp",EDGE,"E2.7.1.0"),sQuery(id+"F0.wireOp",EDGE,"E2.7.1.1"),sQuery(id+"F0.wireOp",EDGE,"E2.7.1.2"),sQuery(id+"F0.wireOp",EDGE,"E2.7.1.3"),sQuery(id+"F0.wireOp",EDGE,"E2.7.2.0"),sQuery(id+"F0.wireOp",EDGE,"E2.7.2.1"),sQuery(id+"F0.wireOp",EDGE,"E2.7.2.2"),sQuery(id+"F0.wireOp",EDGE,"E2.7.2.3"),sQuery(id+"F0.wireOp",EDGE,"E2.7.3.0"),sQuery(id+"F0.wireOp",EDGE,"E2.7.3.1"),sQuery(id+"F0.wireOp",EDGE,"E2.7.3.2"),sQuery(id+"F0.wireOp",EDGE,"E2.7.3.3"),sQuery(id+"F0.wireOp",EDGE,"E2.7.4.0"),sQuery(id+"F0.wireOp",EDGE,"E2.7.4.1"),sQuery(id+"F0.wireOp",EDGE,"E2.7.4.2"),sQuery(id+"F0.wireOp",EDGE,"E2.7.4.3"),sQuery(id+"F0.wireOp",EDGE,"E2.7.5.0"),sQuery(id+"F0.wireOp",EDGE,"E2.7.5.1"),sQuery(id+"F0.wireOp",EDGE,"E2.7.5.2"),sQuery(id+"F0.wireOp",EDGE,"E2.7.5.3"),sQuery(id+"F0.wireOp",EDGE,"E2.7.6.0"),sQuery(id+"F0.wireOp",EDGE,"E2.7.6.1"),sQuery(id+"F0.wireOp",EDGE,"E2.7.6.2"),sQuery(id+"F0.wireOp",EDGE,"E2.7.6.3"),sQuery(id+"F0.wireOp",EDGE,"E2.7.7.0"),sQuery(id+"F0.wireOp",EDGE,"E2.7.7.1"),sQuery(id+"F0.wireOp",EDGE,"E2.7.7.2"),sQuery(id+"F0.wireOp",EDGE,"E2.7.7.3"),sQuery(id+"F0.wireOp",EDGE,"E2.7.8.0"),sQuery(id+"F0.wireOp",EDGE,"E2.7.8.1"),sQuery(id+"F0.wireOp",EDGE,"E2.7.8.2"),sQuery(id+"F0.wireOp",EDGE,"E2.7.8.3"),sQuery(id+"F0.wireOp",EDGE,"E2.7.9.0"),sQuery(id+"F0.wireOp",EDGE,"E2.7.9.1"),sQuery(id+"F0.wireOp",EDGE,"E2.7.9.2"),sQuery(id+"F0.wireOp",EDGE,"E2.7.9.3"),sQuery(id+"F0.wireOp",EDGE,"E2.7.10.0"),sQuery(id+"F0.wireOp",EDGE,"E2.7.10.1"),sQuery(id+"F0.wireOp",EDGE,"E2.7.10.2"),sQuery(id+"F0.wireOp",EDGE,"E2.7.10.3"),sQuery(id+"F0.wireOp",EDGE,"E2.7.11.0"),sQuery(id+"F0.wireOp",EDGE,"E2.7.11.1"),sQuery(id+"F0.wireOp",EDGE,"E2.7.11.2"),sQuery(id+"F0.wireOp",EDGE,"E2.7.11.3"),sQuery(id+"F0.wireOp",EDGE,"E2.7.12.0"),sQuery(id+"F0.wireOp",EDGE,"E2.7.12.1"),sQuery(id+"F0.wireOp",EDGE,"E2.7.12.2"),sQuery(id+"F0.wireOp",EDGE,"E2.7.12.3"),sQuery(id+"F0.wireOp",EDGE,"E2.7.13.0"),sQuery(id+"F0.wireOp",EDGE,"E2.7.13.1"),sQuery(id+"F0.wireOp",EDGE,"E2.7.13.2"),sQuery(id+"F0.wireOp",EDGE,"E2.7.13.3"),sQuery(id+"F0.wireOp",EDGE,"E2.8.0.0"),sQuery(id+"F0.wireOp",EDGE,"E2.8.0.1"),sQuery(id+"F0.wireOp",EDGE,"E2.8.0.2"),sQuery(id+"F0.wireOp",EDGE,"E2.8.0.3"),sQuery(id+"F0.wireOp",EDGE,"E2.8.1.0"),sQuery(id+"F0.wireOp",EDGE,"E2.8.1.1"),sQuery(id+"F0.wireOp",EDGE,"E2.8.1.2"),sQuery(id+"F0.wireOp",EDGE,"E2.8.1.3"),sQuery(id+"F0.wireOp",EDGE,"E2.8.2.0"),sQuery(id+"F0.wireOp",EDGE,"E2.8.2.1"),sQuery(id+"F0.wireOp",EDGE,"E2.8.2.2"),sQuery(id+"F0.wireOp",EDGE,"E2.8.2.3"),sQuery(id+"F0.wireOp",EDGE,"E2.8.3.0"),sQuery(id+"F0.wireOp",EDGE,"E2.8.3.1"),sQuery(id+"F0.wireOp",EDGE,"E2.8.3.2"),sQuery(id+"F0.wireOp",EDGE,"E2.8.3.3"),sQuery(id+"F0.wireOp",EDGE,"E2.8.4.0"),sQuery(id+"F0.wireOp",EDGE,"E2.8.4.1"),sQuery(id+"F0.wireOp",EDGE,"E2.8.4.2"),sQuery(id+"F0.wireOp",EDGE,"E2.8.4.3"),sQuery(id+"F0.wireOp",EDGE,"E2.8.5.0"),sQuery(id+"F0.wireOp",EDGE,"E2.8.5.1"),sQuery(id+"F0.wireOp",EDGE,"E2.8.5.2"),sQuery(id+"F0.wireOp",EDGE,"E2.8.5.3"),sQuery(id+"F0.wireOp",EDGE,"E2.8.6.0"),sQuery(id+"F0.wireOp",EDGE,"E2.8.6.1"),sQuery(id+"F0.wireOp",EDGE,"E2.8.6.2"),sQuery(id+"F0.wireOp",EDGE,"E2.8.6.3"),sQuery(id+"F0.wireOp",EDGE,"E2.8.7.0"),sQuery(id+"F0.wireOp",EDGE,"E2.8.7.1"),sQuery(id+"F0.wireOp",EDGE,"E2.8.7.2"),sQuery(id+"F0.wireOp",EDGE,"E2.8.7.3"),sQuery(id+"F0.wireOp",EDGE,"E2.8.8.0"),sQuery(id+"F0.wireOp",EDGE,"E2.8.8.1"),sQuery(id+"F0.wireOp",EDGE,"E2.8.8.2"),sQuery(id+"F0.wireOp",EDGE,"E2.8.8.3"),sQuery(id+"F0.wireOp",EDGE,"E2.8.9.0"),sQuery(id+"F0.wireOp",EDGE,"E2.8.9.1"),sQuery(id+"F0.wireOp",EDGE,"E2.8.9.2"),sQuery(id+"F0.wireOp",EDGE,"E2.8.9.3"),sQuery(id+"F0.wireOp",EDGE,"E2.8.10.0"),sQuery(id+"F0.wireOp",EDGE,"E2.8.10.1"),sQuery(id+"F0.wireOp",EDGE,"E2.8.10.2"),sQuery(id+"F0.wireOp",EDGE,"E2.8.10.3"),sQuery(id+"F0.wireOp",EDGE,"E2.8.11.0"),sQuery(id+"F0.wireOp",EDGE,"E2.8.11.1"),sQuery(id+"F0.wireOp",EDGE,"E2.8.11.2"),sQuery(id+"F0.wireOp",EDGE,"E2.8.11.3"),sQuery(id+"F0.wireOp",EDGE,"E2.8.12.0"),sQuery(id+"F0.wireOp",EDGE,"E2.8.12.1"),sQuery(id+"F0.wireOp",EDGE,"E2.8.12.2"),sQuery(id+"F0.wireOp",EDGE,"E2.8.12.3"),sQuery(id+"F0.wireOp",EDGE,"E2.8.13.0"),sQuery(id+"F0.wireOp",EDGE,"E2.8.13.1"),sQuery(id+"F0.wireOp",EDGE,"E2.8.13.2"),sQuery(id+"F0.wireOp",EDGE,"E2.8.13.3"),sQuery(id+"F0.wireOp",EDGE,"E2.9.0.0"),sQuery(id+"F0.wireOp",EDGE,"E2.9.0.1"),sQuery(id+"F0.wireOp",EDGE,"E2.9.0.2"),sQuery(id+"F0.wireOp",EDGE,"E2.9.0.3"),sQuery(id+"F0.wireOp",EDGE,"E2.9.1.0"),sQuery(id+"F0.wireOp",EDGE,"E2.9.1.1"),sQuery(id+"F0.wireOp",EDGE,"E2.9.1.2"),sQuery(id+"F0.wireOp",EDGE,"E2.9.1.3"),sQuery(id+"F0.wireOp",EDGE,"E2.9.2.0"),sQuery(id+"F0.wireOp",EDGE,"E2.9.2.1"),sQuery(id+"F0.wireOp",EDGE,"E2.9.2.2"),sQuery(id+"F0.wireOp",EDGE,"E2.9.2.3"),sQuery(id+"F0.wireOp",EDGE,"E2.9.3.0"),sQuery(id+"F0.wireOp",EDGE,"E2.9.3.1"),sQuery(id+"F0.wireOp",EDGE,"E2.9.3.2"),sQuery(id+"F0.wireOp",EDGE,"E2.9.3.3"),sQuery(id+"F0.wireOp",EDGE,"E2.9.4.0"),sQuery(id+"F0.wireOp",EDGE,"E2.9.4.1"),sQuery(id+"F0.wireOp",EDGE,"E2.9.4.2"),sQuery(id+"F0.wireOp",EDGE,"E2.9.4.3"),sQuery(id+"F0.wireOp",EDGE,"E2.9.5.0"),sQuery(id+"F0.wireOp",EDGE,"E2.9.5.1"),sQuery(id+"F0.wireOp",EDGE,"E2.9.5.2"),sQuery(id+"F0.wireOp",EDGE,"E2.9.5.3"),sQuery(id+"F0.wireOp",EDGE,"E2.9.6.0"),sQuery(id+"F0.wireOp",EDGE,"E2.9.6.1"),sQuery(id+"F0.wireOp",EDGE,"E2.9.6.2"),sQuery(id+"F0.wireOp",EDGE,"E2.9.6.3"),sQuery(id+"F0.wireOp",EDGE,"E2.9.7.0"),sQuery(id+"F0.wireOp",EDGE,"E2.9.7.1"),sQuery(id+"F0.wireOp",EDGE,"E2.9.7.2"),sQuery(id+"F0.wireOp",EDGE,"E2.9.7.3"),sQuery(id+"F0.wireOp",EDGE,"E2.9.8.0"),sQuery(id+"F0.wireOp",EDGE,"E2.9.8.1"),sQuery(id+"F0.wireOp",EDGE,"E2.9.8.2"),sQuery(id+"F0.wireOp",EDGE,"E2.9.8.3"),sQuery(id+"F0.wireOp",EDGE,"E2.9.9.0"),sQuery(id+"F0.wireOp",EDGE,"E2.9.9.1"),sQuery(id+"F0.wireOp",EDGE,"E2.9.9.2"),sQuery(id+"F0.wireOp",EDGE,"E2.9.9.3"),sQuery(id+"F0.wireOp",EDGE,"E2.9.10.0"),sQuery(id+"F0.wireOp",EDGE,"E2.9.10.1"),sQuery(id+"F0.wireOp",EDGE,"E2.9.10.2"),sQuery(id+"F0.wireOp",EDGE,"E2.9.10.3"),sQuery(id+"F0.wireOp",EDGE,"E2.9.11.0"),sQuery(id+"F0.wireOp",EDGE,"E2.9.11.1"),sQuery(id+"F0.wireOp",EDGE,"E2.9.11.2"),sQuery(id+"F0.wireOp",EDGE,"E2.9.11.3"),sQuery(id+"F0.wireOp",EDGE,"E2.9.12.0"),sQuery(id+"F0.wireOp",EDGE,"E2.9.12.1"),sQuery(id+"F0.wireOp",EDGE,"E2.9.12.2"),sQuery(id+"F0.wireOp",EDGE,"E2.9.12.3"),sQuery(id+"F0.wireOp",EDGE,"E2.9.13.0"),sQuery(id+"F0.wireOp",EDGE,"E2.9.13.1"),sQuery(id+"F0.wireOp",EDGE,"E2.9.13.2"),sQuery(id+"F0.wireOp",EDGE,"E2.9.13.3"),sQuery(id+"F0.wireOp",EDGE,"E2.10.0.0"),sQuery(id+"F0.wireOp",EDGE,"E2.10.0.1"),sQuery(id+"F0.wireOp",EDGE,"E2.10.0.2"),sQuery(id+"F0.wireOp",EDGE,"E2.10.0.3"),sQuery(id+"F0.wireOp",EDGE,"E2.10.1.0"),sQuery(id+"F0.wireOp",EDGE,"E2.10.1.1"),sQuery(id+"F0.wireOp",EDGE,"E2.10.1.2"),sQuery(id+"F0.wireOp",EDGE,"E2.10.1.3"),sQuery(id+"F0.wireOp",EDGE,"E2.10.2.0"),sQuery(id+"F0.wireOp",EDGE,"E2.10.2.1"),sQuery(id+"F0.wireOp",EDGE,"E2.10.2.2"),sQuery(id+"F0.wireOp",EDGE,"E2.10.2.3"),sQuery(id+"F0.wireOp",EDGE,"E2.10.3.0"),sQuery(id+"F0.wireOp",EDGE,"E2.10.3.1"),sQuery(id+"F0.wireOp",EDGE,"E2.10.3.2"),sQuery(id+"F0.wireOp",EDGE,"E2.10.3.3"),sQuery(id+"F0.wireOp",EDGE,"E2.10.4.0"),sQuery(id+"F0.wireOp",EDGE,"E2.10.4.1"),sQuery(id+"F0.wireOp",EDGE,"E2.10.4.2"),sQuery(id+"F0.wireOp",EDGE,"E2.10.4.3"),sQuery(id+"F0.wireOp",EDGE,"E2.10.5.0"),sQuery(id+"F0.wireOp",EDGE,"E2.10.5.1"),sQuery(id+"F0.wireOp",EDGE,"E2.10.5.2"),sQuery(id+"F0.wireOp",EDGE,"E2.10.5.3"),sQuery(id+"F0.wireOp",EDGE,"E2.10.6.0"),sQuery(id+"F0.wireOp",EDGE,"E2.10.6.1"),sQuery(id+"F0.wireOp",EDGE,"E2.10.6.2"),sQuery(id+"F0.wireOp",EDGE,"E2.10.6.3"),sQuery(id+"F0.wireOp",EDGE,"E2.10.7.0"),sQuery(id+"F0.wireOp",EDGE,"E2.10.7.1"),sQuery(id+"F0.wireOp",EDGE,"E2.10.7.2"),sQuery(id+"F0.wireOp",EDGE,"E2.10.7.3"),sQuery(id+"F0.wireOp",EDGE,"E2.10.8.0"),sQuery(id+"F0.wireOp",EDGE,"E2.10.8.1"),sQuery(id+"F0.wireOp",EDGE,"E2.10.8.2"),sQuery(id+"F0.wireOp",EDGE,"E2.10.8.3"),sQuery(id+"F0.wireOp",EDGE,"E2.10.9.0"),sQuery(id+"F0.wireOp",EDGE,"E2.10.9.1"),sQuery(id+"F0.wireOp",EDGE,"E2.10.9.2"),sQuery(id+"F0.wireOp",EDGE,"E2.10.9.3"),sQuery(id+"F0.wireOp",EDGE,"E2.10.10.0"),sQuery(id+"F0.wireOp",EDGE,"E2.10.10.1"),sQuery(id+"F0.wireOp",EDGE,"E2.10.10.2"),sQuery(id+"F0.wireOp",EDGE,"E2.10.10.3"),sQuery(id+"F0.wireOp",EDGE,"E2.10.11.0"),sQuery(id+"F0.wireOp",EDGE,"E2.10.11.1"),sQuery(id+"F0.wireOp",EDGE,"E2.10.11.2"),sQuery(id+"F0.wireOp",EDGE,"E2.10.11.3"),sQuery(id+"F0.wireOp",EDGE,"E2.10.12.0"),sQuery(id+"F0.wireOp",EDGE,"E2.10.12.1"),sQuery(id+"F0.wireOp",EDGE,"E2.10.12.2"),sQuery(id+"F0.wireOp",EDGE,"E2.10.12.3"),sQuery(id+"F0.wireOp",EDGE,"E2.10.13.0"),sQuery(id+"F0.wireOp",EDGE,"E2.10.13.1"),sQuery(id+"F0.wireOp",EDGE,"E2.10.13.2"),sQuery(id+"F0.wireOp",EDGE,"E2.10.13.3"),sQuery(id+"F0.wireOp",EDGE,"E2.11.0.0"),sQuery(id+"F0.wireOp",EDGE,"E2.11.0.1"),sQuery(id+"F0.wireOp",EDGE,"E2.11.0.2"),sQuery(id+"F0.wireOp",EDGE,"E2.11.0.3"),sQuery(id+"F0.wireOp",EDGE,"E2.11.1.0"),sQuery(id+"F0.wireOp",EDGE,"E2.11.1.1"),sQuery(id+"F0.wireOp",EDGE,"E2.11.1.2"),sQuery(id+"F0.wireOp",EDGE,"E2.11.1.3"),sQuery(id+"F0.wireOp",EDGE,"E2.11.2.0"),sQuery(id+"F0.wireOp",EDGE,"E2.11.2.1"),sQuery(id+"F0.wireOp",EDGE,"E2.11.2.2"),sQuery(id+"F0.wireOp",EDGE,"E2.11.2.3"),sQuery(id+"F0.wireOp",EDGE,"E2.11.3.0"),sQuery(id+"F0.wireOp",EDGE,"E2.11.3.1"),sQuery(id+"F0.wireOp",EDGE,"E2.11.3.2"),sQuery(id+"F0.wireOp",EDGE,"E2.11.3.3"),sQuery(id+"F0.wireOp",EDGE,"E2.11.4.0"),sQuery(id+"F0.wireOp",EDGE,"E2.11.4.1"),sQuery(id+"F0.wireOp",EDGE,"E2.11.4.2"),sQuery(id+"F0.wireOp",EDGE,"E2.11.4.3"),sQuery(id+"F0.wireOp",EDGE,"E2.11.5.0"),sQuery(id+"F0.wireOp",EDGE,"E2.11.5.1"),sQuery(id+"F0.wireOp",EDGE,"E2.11.5.2"),sQuery(id+"F0.wireOp",EDGE,"E2.11.5.3"),sQuery(id+"F0.wireOp",EDGE,"E2.11.6.0"),sQuery(id+"F0.wireOp",EDGE,"E2.11.6.1"),sQuery(id+"F0.wireOp",EDGE,"E2.11.6.2"),sQuery(id+"F0.wireOp",EDGE,"E2.11.6.3"),sQuery(id+"F0.wireOp",EDGE,"E2.11.7.0"),sQuery(id+"F0.wireOp",EDGE,"E2.11.7.1"),sQuery(id+"F0.wireOp",EDGE,"E2.11.7.2"),sQuery(id+"F0.wireOp",EDGE,"E2.11.7.3"),sQuery(id+"F0.wireOp",EDGE,"E2.11.8.0"),sQuery(id+"F0.wireOp",EDGE,"E2.11.8.1"),sQuery(id+"F0.wireOp",EDGE,"E2.11.8.2"),sQuery(id+"F0.wireOp",EDGE,"E2.11.8.3"),sQuery(id+"F0.wireOp",EDGE,"E2.11.9.0"),sQuery(id+"F0.wireOp",EDGE,"E2.11.9.1"),sQuery(id+"F0.wireOp",EDGE,"E2.11.9.2"),sQuery(id+"F0.wireOp",EDGE,"E2.11.9.3"),sQuery(id+"F0.wireOp",EDGE,"E2.11.10.0"),sQuery(id+"F0.wireOp",EDGE,"E2.11.10.1"),sQuery(id+"F0.wireOp",EDGE,"E2.11.10.2"),sQuery(id+"F0.wireOp",EDGE,"E2.11.10.3"),sQuery(id+"F0.wireOp",EDGE,"E2.11.11.0"),sQuery(id+"F0.wireOp",EDGE,"E2.11.11.1"),sQuery(id+"F0.wireOp",EDGE,"E2.11.11.2"),sQuery(id+"F0.wireOp",EDGE,"E2.11.11.3"),sQuery(id+"F0.wireOp",EDGE,"E2.11.12.0"),sQuery(id+"F0.wireOp",EDGE,"E2.11.12.1"),sQuery(id+"F0.wireOp",EDGE,"E2.11.12.2"),sQuery(id+"F0.wireOp",EDGE,"E2.11.12.3"),sQuery(id+"F0.wireOp",EDGE,"E2.11.13.0"),sQuery(id+"F0.wireOp",EDGE,"E2.11.13.1"),sQuery(id+"F0.wireOp",EDGE,"E2.11.13.2"),sQuery(id+"F0.wireOp",EDGE,"E2.11.13.3"),sQuery(id+"F0.wireOp",EDGE,"E2.12.0.0"),sQuery(id+"F0.wireOp",EDGE,"E2.12.0.1"),sQuery(id+"F0.wireOp",EDGE,"E2.12.0.2"),sQuery(id+"F0.wireOp",EDGE,"E2.12.0.3"),sQuery(id+"F0.wireOp",EDGE,"E2.12.1.0"),sQuery(id+"F0.wireOp",EDGE,"E2.12.1.1"),sQuery(id+"F0.wireOp",EDGE,"E2.12.1.2"),sQuery(id+"F0.wireOp",EDGE,"E2.12.1.3"),sQuery(id+"F0.wireOp",EDGE,"E2.12.2.0"),sQuery(id+"F0.wireOp",EDGE,"E2.12.2.1"),sQuery(id+"F0.wireOp",EDGE,"E2.12.2.2"),sQuery(id+"F0.wireOp",EDGE,"E2.12.2.3"),sQuery(id+"F0.wireOp",EDGE,"E2.12.3.0"),sQuery(id+"F0.wireOp",EDGE,"E2.12.3.1"),sQuery(id+"F0.wireOp",EDGE,"E2.12.3.2"),sQuery(id+"F0.wireOp",EDGE,"E2.12.3.3"),sQuery(id+"F0.wireOp",EDGE,"E2.12.4.0"),sQuery(id+"F0.wireOp",EDGE,"E2.12.4.1"),sQuery(id+"F0.wireOp",EDGE,"E2.12.4.2"),sQuery(id+"F0.wireOp",EDGE,"E2.12.4.3"),sQuery(id+"F0.wireOp",EDGE,"E2.12.5.0"),sQuery(id+"F0.wireOp",EDGE,"E2.12.5.1"),sQuery(id+"F0.wireOp",EDGE,"E2.12.5.2"),sQuery(id+"F0.wireOp",EDGE,"E2.12.5.3"),sQuery(id+"F0.wireOp",EDGE,"E2.12.6.0"),sQuery(id+"F0.wireOp",EDGE,"E2.12.6.1"),sQuery(id+"F0.wireOp",EDGE,"E2.12.6.2"),sQuery(id+"F0.wireOp",EDGE,"E2.12.6.3"),sQuery(id+"F0.wireOp",EDGE,"E2.12.7.0"),sQuery(id+"F0.wireOp",EDGE,"E2.12.7.1"),sQuery(id+"F0.wireOp",EDGE,"E2.12.7.2"),sQuery(id+"F0.wireOp",EDGE,"E2.12.7.3"),sQuery(id+"F0.wireOp",EDGE,"E2.12.8.0"),sQuery(id+"F0.wireOp",EDGE,"E2.12.8.1"),sQuery(id+"F0.wireOp",EDGE,"E2.12.8.2"),sQuery(id+"F0.wireOp",EDGE,"E2.12.8.3"),sQuery(id+"F0.wireOp",EDGE,"E2.12.9.0"),sQuery(id+"F0.wireOp",EDGE,"E2.12.9.1"),sQuery(id+"F0.wireOp",EDGE,"E2.12.9.2"),sQuery(id+"F0.wireOp",EDGE,"E2.12.9.3"),sQuery(id+"F0.wireOp",EDGE,"E2.12.10.0"),sQuery(id+"F0.wireOp",EDGE,"E2.12.10.1"),sQuery(id+"F0.wireOp",EDGE,"E2.12.10.2"),sQuery(id+"F0.wireOp",EDGE,"E2.12.10.3"),sQuery(id+"F0.wireOp",EDGE,"E2.12.11.0"),sQuery(id+"F0.wireOp",EDGE,"E2.12.11.1"),sQuery(id+"F0.wireOp",EDGE,"E2.12.11.2"),sQuery(id+"F0.wireOp",EDGE,"E2.12.11.3"),sQuery(id+"F0.wireOp",EDGE,"E2.12.12.0"),sQuery(id+"F0.wireOp",EDGE,"E2.12.12.1"),sQuery(id+"F0.wireOp",EDGE,"E2.12.12.2"),sQuery(id+"F0.wireOp",EDGE,"E2.12.12.3"),sQuery(id+"F0.wireOp",EDGE,"E2.12.13.0"),sQuery(id+"F0.wireOp",EDGE,"E2.12.13.1"),sQuery(id+"F0.wireOp",EDGE,"E2.12.13.2"),sQuery(id+"F0.wireOp",EDGE,"E2.12.13.3"),sQuery(id+"F0.wireOp",EDGE,"E2.13.0.0"),sQuery(id+"F0.wireOp",EDGE,"E2.13.0.1"),sQuery(id+"F0.wireOp",EDGE,"E2.13.0.2"),sQuery(id+"F0.wireOp",EDGE,"E2.13.0.3"),sQuery(id+"F0.wireOp",EDGE,"E2.13.1.0"),sQuery(id+"F0.wireOp",EDGE,"E2.13.1.1"),sQuery(id+"F0.wireOp",EDGE,"E2.13.1.2"),sQuery(id+"F0.wireOp",EDGE,"E2.13.1.3"),sQuery(id+"F0.wireOp",EDGE,"E2.13.2.0"),sQuery(id+"F0.wireOp",EDGE,"E2.13.2.1"),sQuery(id+"F0.wireOp",EDGE,"E2.13.2.2"),sQuery(id+"F0.wireOp",EDGE,"E2.13.2.3"),sQuery(id+"F0.wireOp",EDGE,"E2.13.3.0"),sQuery(id+"F0.wireOp",EDGE,"E2.13.3.1"),sQuery(id+"F0.wireOp",EDGE,"E2.13.3.2"),sQuery(id+"F0.wireOp",EDGE,"E2.13.3.3"),sQuery(id+"F0.wireOp",EDGE,"E2.13.4.0"),sQuery(id+"F0.wireOp",EDGE,"E2.13.4.1"),sQuery(id+"F0.wireOp",EDGE,"E2.13.4.2"),sQuery(id+"F0.wireOp",EDGE,"E2.13.4.3"),sQuery(id+"F0.wireOp",EDGE,"E2.13.5.0"),sQuery(id+"F0.wireOp",EDGE,"E2.13.5.1"),sQuery(id+"F0.wireOp",EDGE,"E2.13.5.2"),sQuery(id+"F0.wireOp",EDGE,"E2.13.5.3"),sQuery(id+"F0.wireOp",EDGE,"E2.13.6.0"),sQuery(id+"F0.wireOp",EDGE,"E2.13.6.1"),sQuery(id+"F0.wireOp",EDGE,"E2.13.6.2"),sQuery(id+"F0.wireOp",EDGE,"E2.13.6.3"),sQuery(id+"F0.wireOp",EDGE,"E2.13.7.0"),sQuery(id+"F0.wireOp",EDGE,"E2.13.7.1"),sQuery(id+"F0.wireOp",EDGE,"E2.13.7.2"),sQuery(id+"F0.wireOp",EDGE,"E2.13.7.3"),sQuery(id+"F0.wireOp",EDGE,"E2.13.8.0"),sQuery(id+"F0.wireOp",EDGE,"E2.13.8.1"),sQuery(id+"F0.wireOp",EDGE,"E2.13.8.2"),sQuery(id+"F0.wireOp",EDGE,"E2.13.8.3"),sQuery(id+"F0.wireOp",EDGE,"E2.13.9.0"),sQuery(id+"F0.wireOp",EDGE,"E2.13.9.1"),sQuery(id+"F0.wireOp",EDGE,"E2.13.9.2"),sQuery(id+"F0.wireOp",EDGE,"E2.13.9.3"),sQuery(id+"F0.wireOp",EDGE,"E2.13.10.0"),sQuery(id+"F0.wireOp",EDGE,"E2.13.10.1"),sQuery(id+"F0.wireOp",EDGE,"E2.13.10.2"),sQuery(id+"F0.wireOp",EDGE,"E2.13.10.3"),sQuery(id+"F0.wireOp",EDGE,"E2.13.11.0"),sQuery(id+"F0.wireOp",EDGE,"E2.13.11.1"),sQuery(id+"F0.wireOp",EDGE,"E2.13.11.2"),sQuery(id+"F0.wireOp",EDGE,"E2.13.11.3"),sQuery(id+"F0.wireOp",EDGE,"E2.13.12.0"),sQuery(id+"F0.wireOp",EDGE,"E2.13.12.1"),sQuery(id+"F0.wireOp",EDGE,"E2.13.12.2"),sQuery(id+"F0.wireOp",EDGE,"E2.13.12.3"),sQuery(id+"F0.wireOp",EDGE,"E2.13.13.0"),sQuery(id+"F0.wireOp",EDGE,"E2.13.13.1"),sQuery(id+"F0.wireOp",EDGE,"E2.13.13.2"),sQuery(id+"F0.wireOp",EDGE,"E2.13.13.3")])],"isStart":false});
            var sketch = newSketch(context, id + "F2", { "sketchPlane" : qUnion([Q0])});
            skLineSegment(sketch, "E3", {"start": v(-138.72, -138.71) * mm, "end": v(1072.04, 1072.05) * mm});
            skLineSegment(sketch, "E4", {"start": v(1072.04, 1072.05) * mm, "end": v(1072.04, -138.71) * mm});
            skLineSegment(sketch, "E5", {"start": v(1072.04, -138.71) * mm, "end": v(-138.72, -138.71) * mm});
            skPoint(sketch, "E6.orphan", {"position": v(-138.72, -138.71) * mm});
            skSolve(sketch);
        }
        {
            var Q0;
            Q0=makeQuery(id+"F2.imprint","IMPRINT",FACE,{"disambiguationData":[TD([[makeQuery(id+"F2.imprint","IMPRINT",EDGE,{"derivedFrom":makeQuery(id+"F1.opExtrude","CAP_EDGE",EDGE,{"disambiguationData":[OSD([sQuery(id+"F0.wireOp",EDGE,"E2.2.0.0")])],"isStart":false})}),-1.0]])]});
            var Q1;
            Q1=makeQuery(id+"F2.imprint","IMPRINT",FACE,{"disambiguationData":[TD([[makeQuery(id+"F2.imprint","IMPRINT",EDGE,{"derivedFrom":makeQuery(id+"F1.opExtrude","CAP_EDGE",EDGE,{"disambiguationData":[OSD([sQuery(id+"F0.wireOp",EDGE,"E2.2.1.0")])],"isStart":false})}),-1.0]])]});
            var Q2;
            Q2=makeQuery(id+"F2.imprint","IMPRINT",FACE,{"disambiguationData":[TD([[makeQuery(id+"F2.imprint","IMPRINT",EDGE,{"derivedFrom":makeQuery(id+"F1.opExtrude","CAP_EDGE",EDGE,{"disambiguationData":[OSD([sQuery(id+"F0.wireOp",EDGE,"E2.3.0.0")])],"isStart":false})}),-1.0]])]});
            var Q3;
            Q3=makeQuery(id+"F2.imprint","IMPRINT",FACE,{"disambiguationData":[TD([[makeQuery(id+"F2.imprint","IMPRINT",EDGE,{"derivedFrom":makeQuery(id+"F1.opExtrude","CAP_EDGE",EDGE,{"disambiguationData":[OSD([sQuery(id+"F0.wireOp",EDGE,"E2.3.1.0")])],"isStart":false})}),-1.0]])]});
            var Q4;
            Q4=makeQuery(id+"F2.imprint","IMPRINT",FACE,{"disambiguationData":[TD([[makeQuery(id+"F2.imprint","IMPRINT",EDGE,{"derivedFrom":makeQuery(id+"F1.opExtrude","CAP_EDGE",EDGE,{"disambiguationData":[OSD([sQuery(id+"F0.wireOp",EDGE,"E2.3.2.0")])],"isStart":false})}),-1.0]])]});
            var Q5;
            Q5=makeQuery(id+"F2.imprint","IMPRINT",FACE,{"disambiguationData":[TD([[makeQuery(id+"F2.imprint","IMPRINT",EDGE,{"derivedFrom":makeQuery(id+"F1.opExtrude","CAP_EDGE",EDGE,{"disambiguationData":[OSD([sQuery(id+"F0.wireOp",EDGE,"E2.4.0.0")])],"isStart":false})}),-1.0]])]});
            var Q6;
            Q6=makeQuery(id+"F2.imprint","IMPRINT",FACE,{"disambiguationData":[TD([[makeQuery(id+"F2.imprint","IMPRINT",EDGE,{"derivedFrom":makeQuery(id+"F1.opExtrude","CAP_EDGE",EDGE,{"disambiguationData":[OSD([sQuery(id+"F0.wireOp",EDGE,"E2.4.1.0")])],"isStart":false})}),-1.0]])]});
            var Q7;
            Q7=makeQuery(id+"F2.imprint","IMPRINT",FACE,{"disambiguationData":[TD([[makeQuery(id+"F2.imprint","IMPRINT",EDGE,{"derivedFrom":makeQuery(id+"F1.opExtrude","CAP_EDGE",EDGE,{"disambiguationData":[OSD([sQuery(id+"F0.wireOp",EDGE,"E2.4.2.0")])],"isStart":false})}),-1.0]])]});
            var Q8;
            Q8=makeQuery(id+"F2.imprint","IMPRINT",FACE,{"disambiguationData":[TD([[makeQuery(id+"F2.imprint","IMPRINT",EDGE,{"derivedFrom":makeQuery(id+"F1.opExtrude","CAP_EDGE",EDGE,{"disambiguationData":[OSD([sQuery(id+"F0.wireOp",EDGE,"E2.4.3.0")])],"isStart":false})}),-1.0]])]});
            var Q9;
            Q9=makeQuery(id+"F2.imprint","IMPRINT",FACE,{"disambiguationData":[TD([[makeQuery(id+"F2.imprint","IMPRINT",EDGE,{"derivedFrom":makeQuery(id+"F1.opExtrude","CAP_EDGE",EDGE,{"disambiguationData":[OSD([sQuery(id+"F0.wireOp",EDGE,"E2.5.0.0")])],"isStart":false})}),-1.0]])]});
            var Q10;
            Q10=makeQuery(id+"F2.imprint","IMPRINT",FACE,{"disambiguationData":[TD([[makeQuery(id+"F2.imprint","IMPRINT",EDGE,{"derivedFrom":makeQuery(id+"F1.opExtrude","CAP_EDGE",EDGE,{"disambiguationData":[OSD([sQuery(id+"F0.wireOp",EDGE,"E2.5.1.0")])],"isStart":false})}),-1.0]])]});
            var Q11;
            Q11=makeQuery(id+"F2.imprint","IMPRINT",FACE,{"disambiguationData":[TD([[makeQuery(id+"F2.imprint","IMPRINT",EDGE,{"derivedFrom":makeQuery(id+"F1.opExtrude","CAP_EDGE",EDGE,{"disambiguationData":[OSD([sQuery(id+"F0.wireOp",EDGE,"E2.5.2.0")])],"isStart":false})}),-1.0]])]});
            var Q12;
            Q12=makeQuery(id+"F2.imprint","IMPRINT",FACE,{"disambiguationData":[TD([[makeQuery(id+"F2.imprint","IMPRINT",EDGE,{"derivedFrom":makeQuery(id+"F1.opExtrude","CAP_EDGE",EDGE,{"disambiguationData":[OSD([sQuery(id+"F0.wireOp",EDGE,"E2.5.3.0")])],"isStart":false})}),-1.0]])]});
            var Q13;
            Q13=makeQuery(id+"F2.imprint","IMPRINT",FACE,{"disambiguationData":[TD([[makeQuery(id+"F2.imprint","IMPRINT",EDGE,{"derivedFrom":makeQuery(id+"F1.opExtrude","CAP_EDGE",EDGE,{"disambiguationData":[OSD([sQuery(id+"F0.wireOp",EDGE,"E2.5.4.0")])],"isStart":false})}),-1.0]])]});
            var Q14;
            Q14=makeQuery(id+"F2.imprint","IMPRINT",FACE,{"disambiguationData":[TD([[makeQuery(id+"F2.imprint","IMPRINT",EDGE,{"derivedFrom":makeQuery(id+"F1.opExtrude","CAP_EDGE",EDGE,{"disambiguationData":[OSD([sQuery(id+"F0.wireOp",EDGE,"E2.6.0.0")])],"isStart":false})}),-1.0]])]});
            var Q15;
            Q15=makeQuery(id+"F2.imprint","IMPRINT",FACE,{"disambiguationData":[TD([[makeQuery(id+"F2.imprint","IMPRINT",EDGE,{"derivedFrom":makeQuery(id+"F1.opExtrude","CAP_EDGE",EDGE,{"disambiguationData":[OSD([sQuery(id+"F0.wireOp",EDGE,"E2.6.1.0")])],"isStart":false})}),-1.0]])]});
            var Q16;
            Q16=makeQuery(id+"F2.imprint","IMPRINT",FACE,{"disambiguationData":[TD([[makeQuery(id+"F2.imprint","IMPRINT",EDGE,{"derivedFrom":makeQuery(id+"F1.opExtrude","CAP_EDGE",EDGE,{"disambiguationData":[OSD([sQuery(id+"F0.wireOp",EDGE,"E2.6.2.0")])],"isStart":false})}),-1.0]])]});
            var Q17;
            Q17=makeQuery(id+"F2.imprint","IMPRINT",FACE,{"disambiguationData":[TD([[makeQuery(id+"F2.imprint","IMPRINT",EDGE,{"derivedFrom":makeQuery(id+"F1.opExtrude","CAP_EDGE",EDGE,{"disambiguationData":[OSD([sQuery(id+"F0.wireOp",EDGE,"E2.6.3.0")])],"isStart":false})}),-1.0]])]});
            var Q18;
            Q18=makeQuery(id+"F2.imprint","IMPRINT",FACE,{"disambiguationData":[TD([[makeQuery(id+"F2.imprint","IMPRINT",EDGE,{"derivedFrom":makeQuery(id+"F1.opExtrude","CAP_EDGE",EDGE,{"disambiguationData":[OSD([sQuery(id+"F0.wireOp",EDGE,"E2.6.4.0")])],"isStart":false})}),-1.0]])]});
            var Q19;
            Q19=makeQuery(id+"F2.imprint","IMPRINT",FACE,{"disambiguationData":[TD([[makeQuery(id+"F2.imprint","IMPRINT",EDGE,{"derivedFrom":makeQuery(id+"F1.opExtrude","CAP_EDGE",EDGE,{"disambiguationData":[OSD([sQuery(id+"F0.wireOp",EDGE,"E2.6.5.0")])],"isStart":false})}),-1.0]])]});
            var Q20;
            Q20=makeQuery(id+"F2.imprint","IMPRINT",FACE,{"disambiguationData":[TD([[makeQuery(id+"F2.imprint","IMPRINT",EDGE,{"derivedFrom":makeQuery(id+"F1.opExtrude","CAP_EDGE",EDGE,{"disambiguationData":[OSD([sQuery(id+"F0.wireOp",EDGE,"E2.7.0.0")])],"isStart":false})}),-1.0]])]});
            var Q21;
            Q21=makeQuery(id+"F2.imprint","IMPRINT",FACE,{"disambiguationData":[TD([[makeQuery(id+"F2.imprint","IMPRINT",EDGE,{"derivedFrom":makeQuery(id+"F1.opExtrude","CAP_EDGE",EDGE,{"disambiguationData":[OSD([sQuery(id+"F0.wireOp",EDGE,"E2.7.1.0")])],"isStart":false})}),-1.0]])]});
            var Q22;
            Q22=makeQuery(id+"F2.imprint","IMPRINT",FACE,{"disambiguationData":[TD([[makeQuery(id+"F2.imprint","IMPRINT",EDGE,{"derivedFrom":makeQuery(id+"F1.opExtrude","CAP_EDGE",EDGE,{"disambiguationData":[OSD([sQuery(id+"F0.wireOp",EDGE,"E2.7.2.0")])],"isStart":false})}),-1.0]])]});
            var Q23;
            Q23=makeQuery(id+"F2.imprint","IMPRINT",FACE,{"disambiguationData":[TD([[makeQuery(id+"F2.imprint","IMPRINT",EDGE,{"derivedFrom":makeQuery(id+"F1.opExtrude","CAP_EDGE",EDGE,{"disambiguationData":[OSD([sQuery(id+"F0.wireOp",EDGE,"E2.7.3.0")])],"isStart":false})}),-1.0]])]});
            var Q24;
            Q24=makeQuery(id+"F2.imprint","IMPRINT",FACE,{"disambiguationData":[TD([[makeQuery(id+"F2.imprint","IMPRINT",EDGE,{"derivedFrom":makeQuery(id+"F1.opExtrude","CAP_EDGE",EDGE,{"disambiguationData":[OSD([sQuery(id+"F0.wireOp",EDGE,"E2.7.4.0")])],"isStart":false})}),-1.0]])]});
            var Q25;
            Q25=makeQuery(id+"F2.imprint","IMPRINT",FACE,{"disambiguationData":[TD([[makeQuery(id+"F2.imprint","IMPRINT",EDGE,{"derivedFrom":makeQuery(id+"F1.opExtrude","CAP_EDGE",EDGE,{"disambiguationData":[OSD([sQuery(id+"F0.wireOp",EDGE,"E2.7.5.0")])],"isStart":false})}),-1.0]])]});
            var Q26;
            Q26=makeQuery(id+"F2.imprint","IMPRINT",FACE,{"disambiguationData":[TD([[makeQuery(id+"F2.imprint","IMPRINT",EDGE,{"derivedFrom":makeQuery(id+"F1.opExtrude","CAP_EDGE",EDGE,{"disambiguationData":[OSD([sQuery(id+"F0.wireOp",EDGE,"E2.7.6.0")])],"isStart":false})}),-1.0]])]});
            var Q27;
            Q27=makeQuery(id+"F2.imprint","IMPRINT",FACE,{"disambiguationData":[TD([[makeQuery(id+"F2.imprint","IMPRINT",EDGE,{"derivedFrom":makeQuery(id+"F1.opExtrude","CAP_EDGE",EDGE,{"disambiguationData":[OSD([sQuery(id+"F0.wireOp",EDGE,"E2.8.0.0")])],"isStart":false})}),-1.0]])]});
            var Q28;
            Q28=makeQuery(id+"F2.imprint","IMPRINT",FACE,{"disambiguationData":[TD([[makeQuery(id+"F2.imprint","IMPRINT",EDGE,{"derivedFrom":makeQuery(id+"F1.opExtrude","CAP_EDGE",EDGE,{"disambiguationData":[OSD([sQuery(id+"F0.wireOp",EDGE,"E2.8.1.0")])],"isStart":false})}),-1.0]])]});
            var Q29;
            Q29=makeQuery(id+"F2.imprint","IMPRINT",FACE,{"disambiguationData":[TD([[makeQuery(id+"F2.imprint","IMPRINT",EDGE,{"derivedFrom":makeQuery(id+"F1.opExtrude","CAP_EDGE",EDGE,{"disambiguationData":[OSD([sQuery(id+"F0.wireOp",EDGE,"E2.8.2.0")])],"isStart":false})}),-1.0]])]});
            var Q30;
            Q30=makeQuery(id+"F2.imprint","IMPRINT",FACE,{"disambiguationData":[TD([[makeQuery(id+"F2.imprint","IMPRINT",EDGE,{"derivedFrom":makeQuery(id+"F1.opExtrude","CAP_EDGE",EDGE,{"disambiguationData":[OSD([sQuery(id+"F0.wireOp",EDGE,"E2.8.3.0")])],"isStart":false})}),-1.0]])]});
            var Q31;
            Q31=makeQuery(id+"F2.imprint","IMPRINT",FACE,{"disambiguationData":[TD([[makeQuery(id+"F2.imprint","IMPRINT",EDGE,{"derivedFrom":makeQuery(id+"F1.opExtrude","CAP_EDGE",EDGE,{"disambiguationData":[OSD([sQuery(id+"F0.wireOp",EDGE,"E2.8.4.0")])],"isStart":false})}),-1.0]])]});
            var Q32;
            Q32=makeQuery(id+"F2.imprint","IMPRINT",FACE,{"disambiguationData":[TD([[makeQuery(id+"F2.imprint","IMPRINT",EDGE,{"derivedFrom":makeQuery(id+"F1.opExtrude","CAP_EDGE",EDGE,{"disambiguationData":[OSD([sQuery(id+"F0.wireOp",EDGE,"E2.8.5.0")])],"isStart":false})}),-1.0]])]});
            var Q33;
            Q33=makeQuery(id+"F2.imprint","IMPRINT",FACE,{"disambiguationData":[TD([[makeQuery(id+"F2.imprint","IMPRINT",EDGE,{"derivedFrom":makeQuery(id+"F1.opExtrude","CAP_EDGE",EDGE,{"disambiguationData":[OSD([sQuery(id+"F0.wireOp",EDGE,"E2.8.6.0")])],"isStart":false})}),-1.0]])]});
            var Q34;
            Q34=makeQuery(id+"F2.imprint","IMPRINT",FACE,{"disambiguationData":[TD([[makeQuery(id+"F2.imprint","IMPRINT",EDGE,{"derivedFrom":makeQuery(id+"F1.opExtrude","CAP_EDGE",EDGE,{"disambiguationData":[OSD([sQuery(id+"F0.wireOp",EDGE,"E2.8.7.0")])],"isStart":false})}),-1.0]])]});
            var Q35;
            Q35=makeQuery(id+"F2.imprint","IMPRINT",FACE,{"disambiguationData":[TD([[makeQuery(id+"F2.imprint","IMPRINT",EDGE,{"derivedFrom":makeQuery(id+"F1.opExtrude","CAP_EDGE",EDGE,{"disambiguationData":[OSD([sQuery(id+"F0.wireOp",EDGE,"E2.9.0.0")])],"isStart":false})}),-1.0]])]});
            var Q36;
            Q36=makeQuery(id+"F2.imprint","IMPRINT",FACE,{"disambiguationData":[TD([[makeQuery(id+"F2.imprint","IMPRINT",EDGE,{"derivedFrom":makeQuery(id+"F1.opExtrude","CAP_EDGE",EDGE,{"disambiguationData":[OSD([sQuery(id+"F0.wireOp",EDGE,"E2.9.1.0")])],"isStart":false})}),-1.0]])]});
            var Q37;
            Q37=makeQuery(id+"F2.imprint","IMPRINT",FACE,{"disambiguationData":[TD([[makeQuery(id+"F2.imprint","IMPRINT",EDGE,{"derivedFrom":makeQuery(id+"F1.opExtrude","CAP_EDGE",EDGE,{"disambiguationData":[OSD([sQuery(id+"F0.wireOp",EDGE,"E2.9.2.0")])],"isStart":false})}),-1.0]])]});
            var Q38;
            Q38=makeQuery(id+"F2.imprint","IMPRINT",FACE,{"disambiguationData":[TD([[makeQuery(id+"F2.imprint","IMPRINT",EDGE,{"derivedFrom":makeQuery(id+"F1.opExtrude","CAP_EDGE",EDGE,{"disambiguationData":[OSD([sQuery(id+"F0.wireOp",EDGE,"E2.9.3.0")])],"isStart":false})}),-1.0]])]});
            var Q39;
            Q39=makeQuery(id+"F2.imprint","IMPRINT",FACE,{"disambiguationData":[TD([[makeQuery(id+"F2.imprint","IMPRINT",EDGE,{"derivedFrom":makeQuery(id+"F1.opExtrude","CAP_EDGE",EDGE,{"disambiguationData":[OSD([sQuery(id+"F0.wireOp",EDGE,"E2.9.4.0")])],"isStart":false})}),-1.0]])]});
            var Q40;
            Q40=makeQuery(id+"F2.imprint","IMPRINT",FACE,{"disambiguationData":[TD([[makeQuery(id+"F2.imprint","IMPRINT",EDGE,{"derivedFrom":makeQuery(id+"F1.opExtrude","CAP_EDGE",EDGE,{"disambiguationData":[OSD([sQuery(id+"F0.wireOp",EDGE,"E2.9.5.0")])],"isStart":false})}),-1.0]])]});
            var Q41;
            Q41=makeQuery(id+"F2.imprint","IMPRINT",FACE,{"disambiguationData":[TD([[makeQuery(id+"F2.imprint","IMPRINT",EDGE,{"derivedFrom":makeQuery(id+"F1.opExtrude","CAP_EDGE",EDGE,{"disambiguationData":[OSD([sQuery(id+"F0.wireOp",EDGE,"E2.9.6.0")])],"isStart":false})}),-1.0]])]});
            var Q42;
            Q42=makeQuery(id+"F2.imprint","IMPRINT",FACE,{"disambiguationData":[TD([[makeQuery(id+"F2.imprint","IMPRINT",EDGE,{"derivedFrom":makeQuery(id+"F1.opExtrude","CAP_EDGE",EDGE,{"disambiguationData":[OSD([sQuery(id+"F0.wireOp",EDGE,"E2.9.7.0")])],"isStart":false})}),-1.0]])]});
            var Q43;
            Q43=makeQuery(id+"F2.imprint","IMPRINT",FACE,{"disambiguationData":[TD([[makeQuery(id+"F2.imprint","IMPRINT",EDGE,{"derivedFrom":makeQuery(id+"F1.opExtrude","CAP_EDGE",EDGE,{"disambiguationData":[OSD([sQuery(id+"F0.wireOp",EDGE,"E2.9.8.0")])],"isStart":false})}),-1.0]])]});
            var Q44;
            Q44=makeQuery(id+"F2.imprint","IMPRINT",FACE,{"disambiguationData":[TD([[makeQuery(id+"F2.imprint","IMPRINT",EDGE,{"derivedFrom":makeQuery(id+"F1.opExtrude","CAP_EDGE",EDGE,{"disambiguationData":[OSD([sQuery(id+"F0.wireOp",EDGE,"E2.10.0.0")])],"isStart":false})}),-1.0]])]});
            var Q45;
            Q45=makeQuery(id+"F2.imprint","IMPRINT",FACE,{"disambiguationData":[TD([[makeQuery(id+"F2.imprint","IMPRINT",EDGE,{"derivedFrom":makeQuery(id+"F1.opExtrude","CAP_EDGE",EDGE,{"disambiguationData":[OSD([sQuery(id+"F0.wireOp",EDGE,"E2.10.1.0")])],"isStart":false})}),-1.0]])]});
            var Q46;
            Q46=makeQuery(id+"F2.imprint","IMPRINT",FACE,{"disambiguationData":[TD([[makeQuery(id+"F2.imprint","IMPRINT",EDGE,{"derivedFrom":makeQuery(id+"F1.opExtrude","CAP_EDGE",EDGE,{"disambiguationData":[OSD([sQuery(id+"F0.wireOp",EDGE,"E2.10.2.0")])],"isStart":false})}),-1.0]])]});
            var Q47;
            Q47=makeQuery(id+"F2.imprint","IMPRINT",FACE,{"disambiguationData":[TD([[makeQuery(id+"F2.imprint","IMPRINT",EDGE,{"derivedFrom":makeQuery(id+"F1.opExtrude","CAP_EDGE",EDGE,{"disambiguationData":[OSD([sQuery(id+"F0.wireOp",EDGE,"E2.10.3.0")])],"isStart":false})}),-1.0]])]});
            var Q48;
            Q48=makeQuery(id+"F2.imprint","IMPRINT",FACE,{"disambiguationData":[TD([[makeQuery(id+"F2.imprint","IMPRINT",EDGE,{"derivedFrom":makeQuery(id+"F1.opExtrude","CAP_EDGE",EDGE,{"disambiguationData":[OSD([sQuery(id+"F0.wireOp",EDGE,"E2.10.4.0")])],"isStart":false})}),-1.0]])]});
            var Q49;
            Q49=makeQuery(id+"F2.imprint","IMPRINT",FACE,{"disambiguationData":[TD([[makeQuery(id+"F2.imprint","IMPRINT",EDGE,{"derivedFrom":makeQuery(id+"F1.opExtrude","CAP_EDGE",EDGE,{"disambiguationData":[OSD([sQuery(id+"F0.wireOp",EDGE,"E2.10.5.0")])],"isStart":false})}),-1.0]])]});
            var Q50;
            Q50=makeQuery(id+"F2.imprint","IMPRINT",FACE,{"disambiguationData":[TD([[makeQuery(id+"F2.imprint","IMPRINT",EDGE,{"derivedFrom":makeQuery(id+"F1.opExtrude","CAP_EDGE",EDGE,{"disambiguationData":[OSD([sQuery(id+"F0.wireOp",EDGE,"E2.10.6.0")])],"isStart":false})}),-1.0]])]});
            var Q51;
            Q51=makeQuery(id+"F2.imprint","IMPRINT",FACE,{"disambiguationData":[TD([[makeQuery(id+"F2.imprint","IMPRINT",EDGE,{"derivedFrom":makeQuery(id+"F1.opExtrude","CAP_EDGE",EDGE,{"disambiguationData":[OSD([sQuery(id+"F0.wireOp",EDGE,"E2.10.7.0")])],"isStart":false})}),-1.0]])]});
            var Q52;
            Q52=makeQuery(id+"F2.imprint","IMPRINT",FACE,{"disambiguationData":[TD([[makeQuery(id+"F2.imprint","IMPRINT",EDGE,{"derivedFrom":makeQuery(id+"F1.opExtrude","CAP_EDGE",EDGE,{"disambiguationData":[OSD([sQuery(id+"F0.wireOp",EDGE,"E2.10.8.0")])],"isStart":false})}),-1.0]])]});
            var Q53;
            Q53=makeQuery(id+"F2.imprint","IMPRINT",FACE,{"disambiguationData":[TD([[makeQuery(id+"F2.imprint","IMPRINT",EDGE,{"derivedFrom":makeQuery(id+"F1.opExtrude","CAP_EDGE",EDGE,{"disambiguationData":[OSD([sQuery(id+"F0.wireOp",EDGE,"E2.10.9.0")])],"isStart":false})}),-1.0]])]});
            var Q54;
            Q54=makeQuery(id+"F2.imprint","IMPRINT",FACE,{"disambiguationData":[TD([[makeQuery(id+"F2.imprint","IMPRINT",EDGE,{"derivedFrom":makeQuery(id+"F1.opExtrude","CAP_EDGE",EDGE,{"disambiguationData":[OSD([sQuery(id+"F0.wireOp",EDGE,"E2.11.0.0")])],"isStart":false})}),-1.0]])]});
            var Q55;
            Q55=makeQuery(id+"F2.imprint","IMPRINT",FACE,{"disambiguationData":[TD([[makeQuery(id+"F2.imprint","IMPRINT",EDGE,{"derivedFrom":makeQuery(id+"F1.opExtrude","CAP_EDGE",EDGE,{"disambiguationData":[OSD([sQuery(id+"F0.wireOp",EDGE,"E2.11.1.0")])],"isStart":false})}),-1.0]])]});
            var Q56;
            Q56=makeQuery(id+"F2.imprint","IMPRINT",FACE,{"disambiguationData":[TD([[makeQuery(id+"F2.imprint","IMPRINT",EDGE,{"derivedFrom":makeQuery(id+"F1.opExtrude","CAP_EDGE",EDGE,{"disambiguationData":[OSD([sQuery(id+"F0.wireOp",EDGE,"E2.11.2.0")])],"isStart":false})}),-1.0]])]});
            var Q57;
            Q57=makeQuery(id+"F2.imprint","IMPRINT",FACE,{"disambiguationData":[TD([[makeQuery(id+"F2.imprint","IMPRINT",EDGE,{"derivedFrom":makeQuery(id+"F1.opExtrude","CAP_EDGE",EDGE,{"disambiguationData":[OSD([sQuery(id+"F0.wireOp",EDGE,"E2.11.3.0")])],"isStart":false})}),-1.0]])]});
            var Q58;
            Q58=makeQuery(id+"F2.imprint","IMPRINT",FACE,{"disambiguationData":[TD([[makeQuery(id+"F2.imprint","IMPRINT",EDGE,{"derivedFrom":makeQuery(id+"F1.opExtrude","CAP_EDGE",EDGE,{"disambiguationData":[OSD([sQuery(id+"F0.wireOp",EDGE,"E2.11.4.0")])],"isStart":false})}),-1.0]])]});
            var Q59;
            Q59=makeQuery(id+"F2.imprint","IMPRINT",FACE,{"disambiguationData":[TD([[makeQuery(id+"F2.imprint","IMPRINT",EDGE,{"derivedFrom":makeQuery(id+"F1.opExtrude","CAP_EDGE",EDGE,{"disambiguationData":[OSD([sQuery(id+"F0.wireOp",EDGE,"E2.11.5.0")])],"isStart":false})}),-1.0]])]});
            var Q60;
            Q60=makeQuery(id+"F2.imprint","IMPRINT",FACE,{"disambiguationData":[TD([[makeQuery(id+"F2.imprint","IMPRINT",EDGE,{"derivedFrom":makeQuery(id+"F1.opExtrude","CAP_EDGE",EDGE,{"disambiguationData":[OSD([sQuery(id+"F0.wireOp",EDGE,"E2.11.6.0")])],"isStart":false})}),-1.0]])]});
            var Q61;
            Q61=makeQuery(id+"F2.imprint","IMPRINT",FACE,{"disambiguationData":[TD([[makeQuery(id+"F2.imprint","IMPRINT",EDGE,{"derivedFrom":makeQuery(id+"F1.opExtrude","CAP_EDGE",EDGE,{"disambiguationData":[OSD([sQuery(id+"F0.wireOp",EDGE,"E2.11.7.0")])],"isStart":false})}),-1.0]])]});
            var Q62;
            Q62=makeQuery(id+"F2.imprint","IMPRINT",FACE,{"disambiguationData":[TD([[makeQuery(id+"F2.imprint","IMPRINT",EDGE,{"derivedFrom":makeQuery(id+"F1.opExtrude","CAP_EDGE",EDGE,{"disambiguationData":[OSD([sQuery(id+"F0.wireOp",EDGE,"E2.11.8.0")])],"isStart":false})}),-1.0]])]});
            var Q63;
            Q63=makeQuery(id+"F2.imprint","IMPRINT",FACE,{"disambiguationData":[TD([[makeQuery(id+"F2.imprint","IMPRINT",EDGE,{"derivedFrom":makeQuery(id+"F1.opExtrude","CAP_EDGE",EDGE,{"disambiguationData":[OSD([sQuery(id+"F0.wireOp",EDGE,"E2.11.9.0")])],"isStart":false})}),-1.0]])]});
            var Q64;
            Q64=makeQuery(id+"F2.imprint","IMPRINT",FACE,{"disambiguationData":[TD([[makeQuery(id+"F2.imprint","IMPRINT",EDGE,{"derivedFrom":makeQuery(id+"F1.opExtrude","CAP_EDGE",EDGE,{"disambiguationData":[OSD([sQuery(id+"F0.wireOp",EDGE,"E2.11.10.0")])],"isStart":false})}),-1.0]])]});
            var Q65;
            Q65=makeQuery(id+"F2.imprint","IMPRINT",FACE,{"disambiguationData":[TD([[makeQuery(id+"F2.imprint","IMPRINT",EDGE,{"derivedFrom":makeQuery(id+"F1.opExtrude","CAP_EDGE",EDGE,{"disambiguationData":[OSD([sQuery(id+"F0.wireOp",EDGE,"E2.12.0.0")])],"isStart":false})}),-1.0]])]});
            var Q66;
            Q66=makeQuery(id+"F2.imprint","IMPRINT",FACE,{"disambiguationData":[TD([[makeQuery(id+"F2.imprint","IMPRINT",EDGE,{"derivedFrom":makeQuery(id+"F1.opExtrude","CAP_EDGE",EDGE,{"disambiguationData":[OSD([sQuery(id+"F0.wireOp",EDGE,"E2.12.1.0")])],"isStart":false})}),-1.0]])]});
            var Q67;
            Q67=makeQuery(id+"F2.imprint","IMPRINT",FACE,{"disambiguationData":[TD([[makeQuery(id+"F2.imprint","IMPRINT",EDGE,{"derivedFrom":makeQuery(id+"F1.opExtrude","CAP_EDGE",EDGE,{"disambiguationData":[OSD([sQuery(id+"F0.wireOp",EDGE,"E2.12.2.0")])],"isStart":false})}),-1.0]])]});
            var Q68;
            Q68=makeQuery(id+"F2.imprint","IMPRINT",FACE,{"disambiguationData":[TD([[makeQuery(id+"F2.imprint","IMPRINT",EDGE,{"derivedFrom":makeQuery(id+"F1.opExtrude","CAP_EDGE",EDGE,{"disambiguationData":[OSD([sQuery(id+"F0.wireOp",EDGE,"E2.12.3.0")])],"isStart":false})}),-1.0]])]});
            var Q69;
            Q69=makeQuery(id+"F2.imprint","IMPRINT",FACE,{"disambiguationData":[TD([[makeQuery(id+"F2.imprint","IMPRINT",EDGE,{"derivedFrom":makeQuery(id+"F1.opExtrude","CAP_EDGE",EDGE,{"disambiguationData":[OSD([sQuery(id+"F0.wireOp",EDGE,"E2.12.4.0")])],"isStart":false})}),-1.0]])]});
            var Q70;
            Q70=makeQuery(id+"F2.imprint","IMPRINT",FACE,{"disambiguationData":[TD([[makeQuery(id+"F2.imprint","IMPRINT",EDGE,{"derivedFrom":makeQuery(id+"F1.opExtrude","CAP_EDGE",EDGE,{"disambiguationData":[OSD([sQuery(id+"F0.wireOp",EDGE,"E2.12.5.0")])],"isStart":false})}),-1.0]])]});
            var Q71;
            Q71=makeQuery(id+"F2.imprint","IMPRINT",FACE,{"disambiguationData":[TD([[makeQuery(id+"F2.imprint","IMPRINT",EDGE,{"derivedFrom":makeQuery(id+"F1.opExtrude","CAP_EDGE",EDGE,{"disambiguationData":[OSD([sQuery(id+"F0.wireOp",EDGE,"E2.12.6.0")])],"isStart":false})}),-1.0]])]});
            var Q72;
            Q72=makeQuery(id+"F2.imprint","IMPRINT",FACE,{"disambiguationData":[TD([[makeQuery(id+"F2.imprint","IMPRINT",EDGE,{"derivedFrom":makeQuery(id+"F1.opExtrude","CAP_EDGE",EDGE,{"disambiguationData":[OSD([sQuery(id+"F0.wireOp",EDGE,"E2.12.7.0")])],"isStart":false})}),-1.0]])]});
            var Q73;
            Q73=makeQuery(id+"F2.imprint","IMPRINT",FACE,{"disambiguationData":[TD([[makeQuery(id+"F2.imprint","IMPRINT",EDGE,{"derivedFrom":makeQuery(id+"F1.opExtrude","CAP_EDGE",EDGE,{"disambiguationData":[OSD([sQuery(id+"F0.wireOp",EDGE,"E2.12.8.0")])],"isStart":false})}),-1.0]])]});
            var Q74;
            Q74=makeQuery(id+"F2.imprint","IMPRINT",FACE,{"disambiguationData":[TD([[makeQuery(id+"F2.imprint","IMPRINT",EDGE,{"derivedFrom":makeQuery(id+"F1.opExtrude","CAP_EDGE",EDGE,{"disambiguationData":[OSD([sQuery(id+"F0.wireOp",EDGE,"E2.12.9.0")])],"isStart":false})}),-1.0]])]});
            var Q75;
            Q75=makeQuery(id+"F2.imprint","IMPRINT",FACE,{"disambiguationData":[TD([[makeQuery(id+"F2.imprint","IMPRINT",EDGE,{"derivedFrom":makeQuery(id+"F1.opExtrude","CAP_EDGE",EDGE,{"disambiguationData":[OSD([sQuery(id+"F0.wireOp",EDGE,"E2.12.10.0")])],"isStart":false})}),-1.0]])]});
            var Q76;
            Q76=makeQuery(id+"F2.imprint","IMPRINT",FACE,{"disambiguationData":[TD([[makeQuery(id+"F2.imprint","IMPRINT",EDGE,{"derivedFrom":makeQuery(id+"F1.opExtrude","CAP_EDGE",EDGE,{"disambiguationData":[OSD([sQuery(id+"F0.wireOp",EDGE,"E2.12.11.0")])],"isStart":false})}),-1.0]])]});
            var Q77;
            Q77=makeQuery(id+"F2.imprint","IMPRINT",FACE,{"disambiguationData":[TD([[makeQuery(id+"F2.imprint","IMPRINT",EDGE,{"derivedFrom":makeQuery(id+"F1.opExtrude","CAP_EDGE",EDGE,{"disambiguationData":[OSD([sQuery(id+"F0.wireOp",EDGE,"E2.13.0.0")])],"isStart":false})}),-1.0]])]});
            var Q78;
            Q78=makeQuery(id+"F2.imprint","IMPRINT",FACE,{"disambiguationData":[TD([[makeQuery(id+"F2.imprint","IMPRINT",EDGE,{"derivedFrom":makeQuery(id+"F1.opExtrude","CAP_EDGE",EDGE,{"disambiguationData":[OSD([sQuery(id+"F0.wireOp",EDGE,"E2.13.1.0")])],"isStart":false})}),-1.0]])]});
            var Q79;
            Q79=makeQuery(id+"F2.imprint","IMPRINT",FACE,{"disambiguationData":[TD([[makeQuery(id+"F2.imprint","IMPRINT",EDGE,{"derivedFrom":makeQuery(id+"F1.opExtrude","CAP_EDGE",EDGE,{"disambiguationData":[OSD([sQuery(id+"F0.wireOp",EDGE,"E2.13.2.0")])],"isStart":false})}),-1.0]])]});
            var Q80;
            Q80=makeQuery(id+"F2.imprint","IMPRINT",FACE,{"disambiguationData":[TD([[makeQuery(id+"F2.imprint","IMPRINT",EDGE,{"derivedFrom":makeQuery(id+"F1.opExtrude","CAP_EDGE",EDGE,{"disambiguationData":[OSD([sQuery(id+"F0.wireOp",EDGE,"E2.13.3.0")])],"isStart":false})}),-1.0]])]});
            var Q81;
            Q81=makeQuery(id+"F2.imprint","IMPRINT",FACE,{"disambiguationData":[TD([[makeQuery(id+"F2.imprint","IMPRINT",EDGE,{"derivedFrom":makeQuery(id+"F1.opExtrude","CAP_EDGE",EDGE,{"disambiguationData":[OSD([sQuery(id+"F0.wireOp",EDGE,"E2.13.4.0")])],"isStart":false})}),-1.0]])]});
            var Q82;
            Q82=makeQuery(id+"F2.imprint","IMPRINT",FACE,{"disambiguationData":[TD([[makeQuery(id+"F2.imprint","IMPRINT",EDGE,{"derivedFrom":makeQuery(id+"F1.opExtrude","CAP_EDGE",EDGE,{"disambiguationData":[OSD([sQuery(id+"F0.wireOp",EDGE,"E2.13.5.0")])],"isStart":false})}),-1.0]])]});
            var Q83;
            Q83=makeQuery(id+"F2.imprint","IMPRINT",FACE,{"disambiguationData":[TD([[makeQuery(id+"F2.imprint","IMPRINT",EDGE,{"derivedFrom":makeQuery(id+"F1.opExtrude","CAP_EDGE",EDGE,{"disambiguationData":[OSD([sQuery(id+"F0.wireOp",EDGE,"E2.13.6.0")])],"isStart":false})}),-1.0]])]});
            var Q84;
            Q84=makeQuery(id+"F2.imprint","IMPRINT",FACE,{"disambiguationData":[TD([[makeQuery(id+"F2.imprint","IMPRINT",EDGE,{"derivedFrom":makeQuery(id+"F1.opExtrude","CAP_EDGE",EDGE,{"disambiguationData":[OSD([sQuery(id+"F0.wireOp",EDGE,"E2.13.7.0")])],"isStart":false})}),-1.0]])]});
            var Q85;
            Q85=makeQuery(id+"F2.imprint","IMPRINT",FACE,{"disambiguationData":[TD([[makeQuery(id+"F2.imprint","IMPRINT",EDGE,{"derivedFrom":makeQuery(id+"F1.opExtrude","CAP_EDGE",EDGE,{"disambiguationData":[OSD([sQuery(id+"F0.wireOp",EDGE,"E2.13.8.0")])],"isStart":false})}),-1.0]])]});
            var Q86;
            Q86=makeQuery(id+"F2.imprint","IMPRINT",FACE,{"disambiguationData":[TD([[makeQuery(id+"F2.imprint","IMPRINT",EDGE,{"derivedFrom":makeQuery(id+"F1.opExtrude","CAP_EDGE",EDGE,{"disambiguationData":[OSD([sQuery(id+"F0.wireOp",EDGE,"E2.13.9.0")])],"isStart":false})}),-1.0]])]});
            var Q87;
            Q87=makeQuery(id+"F2.imprint","IMPRINT",FACE,{"disambiguationData":[TD([[makeQuery(id+"F2.imprint","IMPRINT",EDGE,{"derivedFrom":makeQuery(id+"F1.opExtrude","CAP_EDGE",EDGE,{"disambiguationData":[OSD([sQuery(id+"F0.wireOp",EDGE,"E2.13.10.0")])],"isStart":false})}),-1.0]])]});
            var Q88;
            Q88=makeQuery(id+"F2.imprint","IMPRINT",FACE,{"disambiguationData":[TD([[makeQuery(id+"F2.imprint","IMPRINT",EDGE,{"derivedFrom":makeQuery(id+"F1.opExtrude","CAP_EDGE",EDGE,{"disambiguationData":[OSD([sQuery(id+"F0.wireOp",EDGE,"E2.13.11.0")])],"isStart":false})}),-1.0]])]});
            var Q89;
            Q89=makeQuery(id+"F2.imprint","IMPRINT",FACE,{"disambiguationData":[TD([[makeQuery(id+"F2.imprint","IMPRINT",EDGE,{"derivedFrom":makeQuery(id+"F1.opExtrude","CAP_EDGE",EDGE,{"disambiguationData":[OSD([sQuery(id+"F0.wireOp",EDGE,"E2.13.12.0")])],"isStart":false})}),-1.0]])]});
            var Q90;
            {var subQ4=makeQuery(id+"F1.opExtrude","CAP_EDGE",EDGE,{"disambiguationData":[OSD([sQuery(id+"F0.wireOp",EDGE,"E1.bottom")])],"isStart":false});Q90=makeQuery(id+"F2.imprint","IMPRINT",FACE,{"disambiguationData":[TD([[makeQuery(id+"F2.imprint","IMPRINT",EDGE,{"derivedFrom":subQ4}),1.0]])]});}
            var Q91;
            {var subQ4=makeQuery(id+"F1.opExtrude","CAP_EDGE",EDGE,{"disambiguationData":[OSD([sQuery(id+"F0.wireOp",EDGE,"E2.1.1.2")])],"isStart":false});Q91=makeQuery(id+"F2.imprint","IMPRINT",FACE,{"disambiguationData":[TD([[makeQuery(id+"F2.imprint","IMPRINT",EDGE,{"derivedFrom":subQ4}),1.0]])]});}
            var Q92;
            {var subQ4=makeQuery(id+"F1.opExtrude","CAP_EDGE",EDGE,{"disambiguationData":[OSD([sQuery(id+"F0.wireOp",EDGE,"E2.2.2.2")])],"isStart":false});Q92=makeQuery(id+"F2.imprint","IMPRINT",FACE,{"disambiguationData":[TD([[makeQuery(id+"F2.imprint","IMPRINT",EDGE,{"derivedFrom":subQ4}),1.0]])]});}
            var Q93;
            {var subQ1=makeQuery(id+"F1.opExtrude","CAP_EDGE",EDGE,{"disambiguationData":[OSD([sQuery(id+"F0.wireOp",EDGE,"E2.3.3.2")])],"isStart":false});Q93=makeQuery(id+"F2.imprint","IMPRINT",FACE,{"disambiguationData":[TD([[makeQuery(id+"F2.imprint","IMPRINT",EDGE,{"derivedFrom":subQ1}),1.0]])]});}
            var Q94;
            {var subQ4=makeQuery(id+"F1.opExtrude","CAP_EDGE",EDGE,{"disambiguationData":[OSD([sQuery(id+"F0.wireOp",EDGE,"E2.4.4.2")])],"isStart":false});Q94=makeQuery(id+"F2.imprint","IMPRINT",FACE,{"disambiguationData":[TD([[makeQuery(id+"F2.imprint","IMPRINT",EDGE,{"derivedFrom":subQ4}),1.0]])]});}
            var Q95;
            {var subQ4=makeQuery(id+"F1.opExtrude","CAP_EDGE",EDGE,{"disambiguationData":[OSD([sQuery(id+"F0.wireOp",EDGE,"E2.5.5.2")])],"isStart":false});Q95=makeQuery(id+"F2.imprint","IMPRINT",FACE,{"disambiguationData":[TD([[makeQuery(id+"F2.imprint","IMPRINT",EDGE,{"derivedFrom":subQ4}),1.0]])]});}
            var Q96;
            {var subQ4=makeQuery(id+"F1.opExtrude","CAP_EDGE",EDGE,{"disambiguationData":[OSD([sQuery(id+"F0.wireOp",EDGE,"E2.6.6.2")])],"isStart":false});Q96=makeQuery(id+"F2.imprint","IMPRINT",FACE,{"disambiguationData":[TD([[makeQuery(id+"F2.imprint","IMPRINT",EDGE,{"derivedFrom":subQ4}),1.0]])]});}
            var Q97;
            {var subQ4=makeQuery(id+"F1.opExtrude","CAP_EDGE",EDGE,{"disambiguationData":[OSD([sQuery(id+"F0.wireOp",EDGE,"E2.7.7.2")])],"isStart":false});Q97=makeQuery(id+"F2.imprint","IMPRINT",FACE,{"disambiguationData":[TD([[makeQuery(id+"F2.imprint","IMPRINT",EDGE,{"derivedFrom":subQ4}),1.0]])]});}
            var Q98;
            {var subQ1=makeQuery(id+"F1.opExtrude","CAP_EDGE",EDGE,{"disambiguationData":[OSD([sQuery(id+"F0.wireOp",EDGE,"E2.8.8.2")])],"isStart":false});Q98=makeQuery(id+"F2.imprint","IMPRINT",FACE,{"disambiguationData":[TD([[makeQuery(id+"F2.imprint","IMPRINT",EDGE,{"derivedFrom":subQ1}),1.0]])]});}
            var Q99;
            {var subQ4=makeQuery(id+"F1.opExtrude","CAP_EDGE",EDGE,{"disambiguationData":[OSD([sQuery(id+"F0.wireOp",EDGE,"E2.9.9.2")])],"isStart":false});Q99=makeQuery(id+"F2.imprint","IMPRINT",FACE,{"disambiguationData":[TD([[makeQuery(id+"F2.imprint","IMPRINT",EDGE,{"derivedFrom":subQ4}),1.0]])]});}
            var Q100;
            {var subQ6=makeQuery(id+"F1.opExtrude","CAP_EDGE",EDGE,{"disambiguationData":[OSD([sQuery(id+"F0.wireOp",EDGE,"E2.10.10.2")])],"isStart":false});Q100=makeQuery(id+"F2.imprint","IMPRINT",FACE,{"disambiguationData":[TD([[makeQuery(id+"F2.imprint","IMPRINT",EDGE,{"derivedFrom":subQ6}),1.0]])]});}
            var Q101;
            {var subQ4=makeQuery(id+"F1.opExtrude","CAP_EDGE",EDGE,{"disambiguationData":[OSD([sQuery(id+"F0.wireOp",EDGE,"E2.11.11.2")])],"isStart":false});Q101=makeQuery(id+"F2.imprint","IMPRINT",FACE,{"disambiguationData":[TD([[makeQuery(id+"F2.imprint","IMPRINT",EDGE,{"derivedFrom":subQ4}),1.0]])]});}
            var Q102;
            {var subQ4=makeQuery(id+"F1.opExtrude","CAP_EDGE",EDGE,{"disambiguationData":[OSD([sQuery(id+"F0.wireOp",EDGE,"E2.12.12.2")])],"isStart":false});Q102=makeQuery(id+"F2.imprint","IMPRINT",FACE,{"disambiguationData":[TD([[makeQuery(id+"F2.imprint","IMPRINT",EDGE,{"derivedFrom":subQ4}),1.0]])]});}
            var Q103;
            {var subQ1=makeQuery(id+"F1.opExtrude","CAP_EDGE",EDGE,{"disambiguationData":[OSD([sQuery(id+"F0.wireOp",EDGE,"E2.13.13.2")])],"isStart":false});Q103=makeQuery(id+"F2.imprint","IMPRINT",FACE,{"disambiguationData":[TD([[makeQuery(id+"F2.imprint","IMPRINT",EDGE,{"derivedFrom":subQ1}),1.0]])]});}
            var Q104;
            {var subQ90=makeQuery(id+"F1.opExtrude","CAP_EDGE",EDGE,{"disambiguationData":[OSD([sQuery(id+"F0.wireOp",EDGE,"E0.bottom")])],"isStart":false});Q104=makeQuery(id+"F2.imprint","IMPRINT",FACE,{"disambiguationData":[TD([[makeQuery(id+"F2.imprint","IMPRINT",EDGE,{"derivedFrom":subQ90}),1.0]])]});}
            extrude(context, id + "F3", {"entities" : qUnion([Q0, Q1, Q2, Q3, Q4, Q5, Q6, Q7, Q8, Q9, Q10, Q11, Q12, Q13, Q14, Q15, Q16, Q17, Q18, Q19, Q20, Q21, Q22, Q23, Q24, Q25, Q26, Q27, Q28, Q29, Q30, Q31, Q32, Q33, Q34, Q35, Q36, Q37, Q38, Q39, Q40, Q41, Q42, Q43, Q44, Q45, Q46, Q47, Q48, Q49, Q50, Q51, Q52, Q53, Q54, Q55, Q56, Q57, Q58, Q59, Q60, Q61, Q62, Q63, Q64, Q65, Q66, Q67, Q68, Q69, Q70, Q71, Q72, Q73, Q74, Q75, Q76, Q77, Q78, Q79, Q80, Q81, Q82, Q83, Q84, Q85, Q86, Q87, Q88, Q89, Q90, Q91, Q92, Q93, Q94, Q95, Q96, Q97, Q98, Q99, Q100, Q101, Q102, Q103, Q104]), "operationType" : NewBodyOperationType.REMOVE, "endBound" : BoundingType.THROUGH_ALL, "oppositeDirection" : true, "depth" : 40 * mm, "offsetDistance" : 25 * mm});
        }
    });
